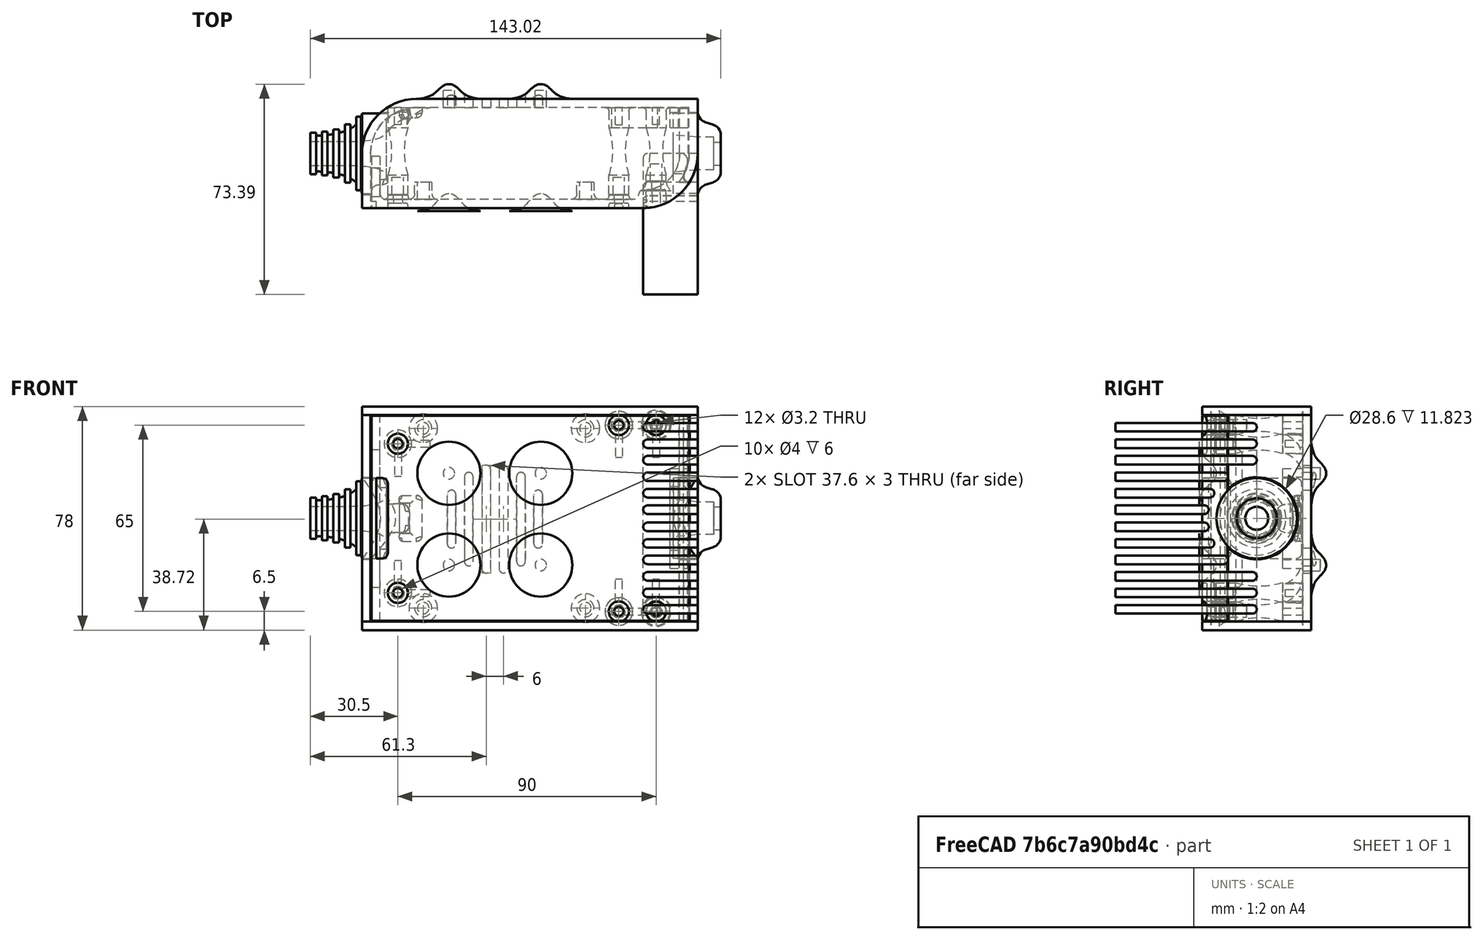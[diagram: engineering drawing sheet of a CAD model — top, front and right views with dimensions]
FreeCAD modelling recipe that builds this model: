
FCSTD DOCUMENT  (FreeCAD 0.19R0.19.2)
Label: enclosure_117
License: All rights reserved
LicenseURL: http://en.wikipedia.org/wiki/All_rights_reserved
objects: Part::Feature×72, Part::Revolution×72, Part::MultiFuse×53, Sketcher::SketchObject×32, Part::Fillet×24, Part::Cylinder×22, Part::Extrusion×21, Part::Cut×21, Part::Box×12, App::MeasureDistance×4
note: 329 computed .brp shape members not serialized (recipe doc carries the construction recipe); baked Part::Feature solids carry a one-line shape summary decoded from their .brp

FEATURE [Sketcher::SketchObject] Sketch  label="topSketch"
  FullyConstrained = true
  sketch-geometry (13):
    g0: LineSegment StartX=117 StartY=19 StartZ=0 EndX=117 EndY=38 EndZ=0
    g1: ArcOfCircle CenterX=98 CenterY=19 CenterZ=0 NormalX=0 NormalY=0 NormalZ=1 AngleXU=0 Radius=19 StartAngle=5.7297 EndAngle=6.28319
    g2: LineSegment StartX=0 StartY=3 StartZ=0 EndX=0 EndY=19 EndZ=0
    g3: LineSegment StartX=19 StartY=38 StartZ=0 EndX=117 EndY=38 EndZ=0
    g4: ArcOfCircle CenterX=19 CenterY=19 CenterZ=0 NormalX=0 NormalY=0 NormalZ=1 AngleXU=0 Radius=19 StartAngle=1.5708 EndAngle=3.14159
    g5: ArcOfCircle CenterX=19 CenterY=19 CenterZ=0 NormalX=0 NormalY=0 NormalZ=1 AngleXU=0 Radius=16 StartAngle=1.5708 EndAngle=3.14159
    g6: ArcOfCircle CenterX=98 CenterY=19 CenterZ=0 NormalX=0 NormalY=0 NormalZ=1 AngleXU=0 Radius=16 StartAngle=5.60905 EndAngle=6.28319
    g7: LineSegment StartX=114 StartY=19 StartZ=0 EndX=114 EndY=35 EndZ=0
    g8: LineSegment StartX=110.5 StartY=9.01251 StartZ=0 EndX=114.163 EndY=9.01251 EndZ=0
    g9: LineSegment StartX=114 StartY=35 StartZ=0 EndX=19 EndY=35 EndZ=0
    g10: LineSegment StartX=0 StartY=3 StartZ=0 EndX=0 EndY=0 EndZ=0
    g11: LineSegment StartX=3 StartY=0 StartZ=0 EndX=0 EndY=0 EndZ=0
    g12: LineSegment StartX=3 StartY=19 StartZ=0 EndX=3 EndY=0 EndZ=0
  constraints (33):
    c: Vertical(g0)
    c: Distance(g0) = 19
    c: Block(g0)
    c: Coincident(g1,g0)
    c: Block(g1)
    c: Vertical(g2)
    c: Block(g2)
    c: Coincident(g3,g0)
    c: Horizontal(g3)
    c: Distance(g3) = 98
    c: Coincident(g4,g3)
    c: Coincident(g4,g2)
    c: Block(g4)
    c: Coincident(g5,g4)
    c: Coincident(g6,g1)
    c: Block(g6)
    c: Block(g5)
    c: Coincident(g7,g6)
    c: Vertical(g7)
    c: Coincident(g8,g6)
    c: Coincident(g8,g1)
    c: Coincident(g9,g7)
    c: Coincident(g9,g5)
    c: Horizontal(g9)
    c: Tangent(g9,g5)
    c: Coincident(g10,g2)
    c: Distance(g10) = 3
    c: Vertical(g10)
    c: Coincident(g11,g10)
    c: Horizontal(g11)
    c: Coincident(g12,g5)
    c: Coincident(g12,g11)
    c: Vertical(g12)
FEATURE [Sketcher::SketchObject] Sketch001  label="bottomSketch"
  FullyConstrained = true
  sketch-geometry (32):
    g0: LineSegment StartX=3.3 StartY=-6.03275e-07 StartZ=0 EndX=98 EndY=-6.03275e-07 EndZ=0
    g1: ArcOfCircle CenterX=98 CenterY=19 CenterZ=0 NormalX=0 NormalY=0 NormalZ=1 AngleXU=0 Radius=19 StartAngle=4.71239 EndAngle=5.71103
    g2: LineSegment StartX=6.3 StartY=8 StartZ=0 EndX=3.3 EndY=8 EndZ=0
    g3: LineSegment StartX=3.3 StartY=8 StartZ=0 EndX=3.3 EndY=-6.03275e-07 EndZ=0
    g4: ArcOfCircle CenterX=8.3 CenterY=5 CenterZ=0 NormalX=0 NormalY=0 NormalZ=1 AngleXU=0 Radius=2 StartAngle=3.14159 EndAngle=4.71239
    g5: LineSegment StartX=6.3 StartY=8 StartZ=0 EndX=6.3 EndY=5 EndZ=0
    g6: ArcOfCircle CenterX=98 CenterY=19 CenterZ=0 NormalX=0 NormalY=0 NormalZ=1 AngleXU=0 Radius=12.7 StartAngle=4.71239 EndAngle=6.28319
    g7: LineSegment StartX=94.7 StartY=3 StartZ=0 EndX=8.3 EndY=3 EndZ=0
    g8-g12: Circle x5 (B-spline internal-alignment scaffolding for g13; pole/knot coordinates omitted)
    g13: BSplineCurve PolesCount=5 KnotsCount=3 Degree=3 IsPeriodic=0
    g14: GeomPoint X=98 Y=6.3 Z=0
    g15: GeomPoint X=96.3938 Y=4.71946 Z=0
    g16: GeomPoint X=94.7 Y=3 Z=0
    g17-g23: Circle x7 (B-spline internal-alignment scaffolding for g24; pole/knot coordinates omitted)
    g24: BSplineCurve PolesCount=7 KnotsCount=5 Degree=3 IsPeriodic=0
    g25-g29: GeomPoint x5 (B-spline internal-alignment scaffolding for g24; pole/knot coordinates omitted)
    g30: ArcOfCircle CenterX=98 CenterY=19 CenterZ=0 NormalX=0 NormalY=0 NormalZ=1 AngleXU=0 Radius=15.7 StartAngle=5.81226 EndAngle=6.28319
    g31: LineSegment StartX=110.7 StartY=19 StartZ=0 EndX=113.7 EndY=19 EndZ=0
  constraints (41):
    c: Horizontal(g0)
    c: Coincident(g1,g0)
    c: Block(g1)
    c: Horizontal(g2)
    c: Distance(g2) = 3
    c: Coincident(g3,g2)
    c: Vertical(g3)
    c: Coincident(g3,g0)
    c: Block(g4)
    c: Block(g2)
    c: Coincident(g5,g2)
    c: Coincident(g5,g4)
    c: Vertical(g5)
    c: Coincident(g6,g1)
    c: Block(g6)
    c: Coincident(g7,g4)
    c: Horizontal(g7)
    c: Block(g0)
    c: Block(g7)
    c: Block(g3)
    c: Coincident(g13,g6)
    c: Weight(g8) = 1
    c: Equal(g8, g9-g12) x4
    c: Coincident(g13,g7)
    c: InternalAlignment(g8-g12 -> g13) x5
    c: InternalAlignment(g14,g13)
    c: InternalAlignment(g15,g13)
    c: InternalAlignment(g16,g13)
    c: Block(g13)
    c: Weight(g17) = 1
    c: Equal(g17, g18-g23) x6
    c: Coincident(g24,g1)
    c: InternalAlignment(g17-g23 -> g24) x7
    c: InternalAlignment(g25-g29 -> g24) x5
    c: Block(g24)
    c: Coincident(g30,g24)
    c: Coincident(g31,g6)
    c: Coincident(g31,g30)
    c: Horizontal(g31)
    c: Block(g31)
    c: Block(g30)
FEATURE [Part::Extrusion] Extrude  label="top"
  Base = -> Sketch
  Dir = (0,0,1)
  DirMode = 2
  FaceMakerClass = Part::FaceMakerBullseye
  LengthFwd = 72
  LengthRev = 0
  Solid = true
  Symmetric = false
FEATURE [Part::Extrusion] Extrude001  label="bottom"
  Base = -> Sketch001
  Dir = (0,0,1)
  DirMode = 2
  FaceMakerClass = Part::FaceMakerBullseye
  LengthFwd = 71.4
  LengthRev = 0
  Placement = pos=(0,0,0.3) rot=(0,0,1;0rad)
  Solid = true
  Symmetric = false
FEATURE [Sketcher::SketchObject] Sketch002  label="topSketch001"
  FullyConstrained = true
  sketch-geometry (6):
    g0: LineSegment StartX=19 StartY=38 StartZ=0 EndX=117 EndY=38 EndZ=0
    g1: ArcOfCircle CenterX=19 CenterY=19 CenterZ=0 NormalX=0 NormalY=0 NormalZ=1 AngleXU=0 Radius=19 StartAngle=1.5708 EndAngle=3.14159
    g2: LineSegment StartX=117 StartY=38 StartZ=0 EndX=117 EndY=19 EndZ=0
    g3: LineSegment StartX=98 StartY=1.0161e-12 StartZ=0 EndX=5.22862e-06 EndY=1.0161e-12 EndZ=0
    g4: LineSegment StartX=5.22862e-06 StartY=19 StartZ=0 EndX=5.22862e-06 EndY=1.0161e-12 EndZ=0
    g5: ArcOfCircle CenterX=98 CenterY=19 CenterZ=0 NormalX=0 NormalY=0 NormalZ=1 AngleXU=0 Radius=19 StartAngle=4.71239 EndAngle=6.28319
  constraints (16):
    c: Horizontal(g0)
    c: Distance(g0) = 98
    c: Coincident(g1,g0)
    c: Block(g1)
    c: Coincident(g2,g0)
    c: Vertical(g2)
    c: Distance(g2) = 19
    c: Horizontal(g3)
    c: Coincident(g4,g1)
    c: Vertical(g4)
    c: Coincident(g3,g4)
    c: Block(g3)
    c: Coincident(g5,g2)
    c: Coincident(g5,g3)
    c: Block(g0)
    c: Block(g5)
FEATURE [Part::Extrusion] Extrude002  label="sideA"
  Base = -> Sketch002
  Dir = (0,0,1)
  DirMode = 2
  FaceMakerClass = Part::FaceMakerBullseye
  LengthFwd = 3
  LengthRev = 0
  Placement = pos=(0,0,-3) rot=(0,0,1;0rad)
  Solid = true
  Symmetric = false
FEATURE [Sketcher::SketchObject] Sketch003  label="topSketch002"
  FullyConstrained = true
  sketch-geometry (6):
    g0: LineSegment StartX=19 StartY=38 StartZ=0 EndX=117 EndY=38 EndZ=0
    g1: ArcOfCircle CenterX=19 CenterY=19 CenterZ=0 NormalX=0 NormalY=0 NormalZ=1 AngleXU=0 Radius=19 StartAngle=1.5708 EndAngle=3.14159
    g2: LineSegment StartX=117 StartY=38 StartZ=0 EndX=117 EndY=19 EndZ=0
    g3: LineSegment StartX=98 StartY=1.0161e-12 StartZ=0 EndX=5.22862e-06 EndY=1.0161e-12 EndZ=0
    g4: LineSegment StartX=5.22862e-06 StartY=19 StartZ=0 EndX=5.22862e-06 EndY=1.0161e-12 EndZ=0
    g5: ArcOfCircle CenterX=98 CenterY=19 CenterZ=0 NormalX=0 NormalY=0 NormalZ=1 AngleXU=0 Radius=19 StartAngle=4.71239 EndAngle=6.28319
  constraints (16):
    c: Horizontal(g0)
    c: Distance(g0) = 98
    c: Coincident(g1,g0)
    c: Block(g1)
    c: Coincident(g2,g0)
    c: Vertical(g2)
    c: Distance(g2) = 19
    c: Horizontal(g3)
    c: Coincident(g4,g1)
    c: Vertical(g4)
    c: Coincident(g3,g4)
    c: Block(g3)
    c: Coincident(g5,g2)
    c: Coincident(g5,g3)
    c: Block(g0)
    c: Block(g5)
FEATURE [Part::Extrusion] Extrude003  label="sideB"
  Base = -> Sketch003
  Dir = (0,0,1)
  DirMode = 2
  FaceMakerClass = Part::FaceMakerBullseye
  LengthFwd = 3
  LengthRev = 0
  Placement = pos=(0,0,72) rot=(0,0,1;0rad)
  Solid = true
  Symmetric = false
FEATURE [Sketcher::SketchObject] Sketch004
  FullyConstrained = true
  MapMode = 3
  Placement = pos=(0,0,0) rot=(1,0,0;1.5708rad)
  Support = -> [Extrude]
  sketch-geometry (8):
    g0: Circle CenterX=80.351 CenterY=-67.6202 CenterZ=0 NormalX=0 NormalY=0 NormalZ=1 AngleXU=0 Radius=2
    g1: Circle CenterX=80.351 CenterY=-67.6202 CenterZ=0 NormalX=0 NormalY=0 NormalZ=1 AngleXU=0 Radius=3
    g2: Circle CenterX=80.351 CenterY=-4.92017 CenterZ=0 NormalX=0 NormalY=0 NormalZ=1 AngleXU=0 Radius=2
    g3: Circle CenterX=80.351 CenterY=-4.92017 CenterZ=0 NormalX=0 NormalY=0 NormalZ=1 AngleXU=0 Radius=3
    g4: Circle CenterX=23.851 CenterY=-4.92017 CenterZ=0 NormalX=0 NormalY=0 NormalZ=1 AngleXU=0 Radius=2
    g5: Circle CenterX=23.851 CenterY=-4.92017 CenterZ=0 NormalX=0 NormalY=0 NormalZ=1 AngleXU=0 Radius=3
    g6: Circle CenterX=23.851 CenterY=-67.6202 CenterZ=0 NormalX=0 NormalY=0 NormalZ=1 AngleXU=0 Radius=2
    g7: Circle CenterX=23.851 CenterY=-67.6202 CenterZ=0 NormalX=0 NormalY=0 NormalZ=1 AngleXU=0 Radius=3
  constraints (8):
    c: Block(g3)
    c: Block(g2)
    c: Block(g1)
    c: Block(g0)
    c: Block(g6)
    c: Block(g7)
    c: Block(g4)
    c: Block(g5)
FEATURE [Part::Extrusion] Extrude004
  Base = -> Sketch004
  Dir = (0,-1,2e-16)
  DirMode = 2
  FaceMakerClass = Part::FaceMakerBullseye
  LengthFwd = 6
  LengthRev = 0
  Placement = pos=(0,9,0) rot=(0,0,1;0rad)
  Solid = true
  Symmetric = false
FEATURE [Sketcher::SketchObject] Sketch005
  FullyConstrained = true
  MapMode = 3
  Placement = pos=(0,0,0) rot=(1,0,0;1.5708rad)
  Support = -> [Extrude]
  sketch-geometry (8):
    g0: Circle CenterX=80.351 CenterY=-67.6202 CenterZ=0 NormalX=0 NormalY=0 NormalZ=1 AngleXU=0 Radius=3
    g1: Circle CenterX=80.351 CenterY=-4.92017 CenterZ=0 NormalX=0 NormalY=0 NormalZ=1 AngleXU=0 Radius=3
    g2: Circle CenterX=23.851 CenterY=-4.92017 CenterZ=0 NormalX=0 NormalY=0 NormalZ=1 AngleXU=0 Radius=3
    g3: Circle CenterX=23.851 CenterY=-67.6202 CenterZ=0 NormalX=0 NormalY=0 NormalZ=1 AngleXU=0 Radius=3
    g4: Circle CenterX=23.851 CenterY=-67.6202 CenterZ=0 NormalX=0 NormalY=0 NormalZ=1 AngleXU=0 Radius=5
    g5: Circle CenterX=80.351 CenterY=-67.6202 CenterZ=0 NormalX=0 NormalY=0 NormalZ=1 AngleXU=0 Radius=5
    g6: Circle CenterX=23.851 CenterY=-4.92017 CenterZ=0 NormalX=0 NormalY=0 NormalZ=1 AngleXU=0 Radius=5
    g7: Circle CenterX=80.351 CenterY=-4.92017 CenterZ=0 NormalX=0 NormalY=0 NormalZ=1 AngleXU=0 Radius=5
  constraints (8):
    c: Block(g1)
    c: Block(g0)
    c: Block(g3)
    c: Block(g2)
    c: Block(g5)
    c: Block(g4)
    c: Block(g6)
    c: Block(g7)
FEATURE [Part::Extrusion] Extrude005
  Base = -> Sketch005
  Dir = (0,-1,2e-16)
  DirMode = 2
  FaceMakerClass = Part::FaceMakerBullseye
  LengthFwd = 2
  LengthRev = 0
  Solid = true
  Symmetric = false
FEATURE [Sketcher::SketchObject] Sketch006
  FullyConstrained = true
  MapMode = 3
  Placement = pos=(0,0,0) rot=(1,0,0;1.5708rad)
  sketch-geometry (8):
    g0: Circle CenterX=80.351 CenterY=-67.6202 CenterZ=0 NormalX=0 NormalY=0 NormalZ=1 AngleXU=0 Radius=3
    g1: Circle CenterX=80.351 CenterY=-4.92017 CenterZ=0 NormalX=0 NormalY=0 NormalZ=1 AngleXU=0 Radius=3
    g2: Circle CenterX=23.851 CenterY=-4.92017 CenterZ=0 NormalX=0 NormalY=0 NormalZ=1 AngleXU=0 Radius=3
    g3: Circle CenterX=23.851 CenterY=-67.6202 CenterZ=0 NormalX=0 NormalY=0 NormalZ=1 AngleXU=0 Radius=3
    g4: Circle CenterX=23.851 CenterY=-67.6202 CenterZ=0 NormalX=0 NormalY=0 NormalZ=1 AngleXU=0 Radius=5
    g5: Circle CenterX=80.351 CenterY=-67.6202 CenterZ=0 NormalX=0 NormalY=0 NormalZ=1 AngleXU=0 Radius=5
    g6: Circle CenterX=23.851 CenterY=-4.92017 CenterZ=0 NormalX=0 NormalY=0 NormalZ=1 AngleXU=0 Radius=5
    g7: Circle CenterX=80.351 CenterY=-4.92017 CenterZ=0 NormalX=0 NormalY=0 NormalZ=1 AngleXU=0 Radius=5
  constraints (8):
    c: Block(g1)
    c: Block(g0)
    c: Block(g3)
    c: Block(g2)
    c: Block(g5)
    c: Block(g4)
    c: Block(g6)
    c: Block(g7)
FEATURE [Part::Extrusion] Extrude007
  Base = -> Sketch006
  Dir = (0,-1,2e-16)
  DirMode = 2
  FaceMakerClass = Part::FaceMakerBullseye
  LengthFwd = 2
  LengthRev = 0
  Solid = true
  Symmetric = false
FEATURE [Part::Fillet] Fillet
  Base = -> Extrude007
  Edges = 4 edges r=1.99: [Edge6,Edge12,Edge18,Edge24]
FEATURE [Part::Cut] Cut
  Base = -> Extrude005
  Placement = pos=(0,5,0) rot=(0,0,1;0rad)
  Tool = -> Fillet
FEATURE [Part::MultiFuse] Fusion  label="pCBScrews"
  Placement = pos=(-2.5,0,72.3) rot=(0,0,1;0rad)
  Shapes = -> [Extrude004,Cut]
FEATURE [App::MeasureDistance] Distance  label="Distance: 0.69 mm"
  Distance = 0.685967
  P1 = (24.0138,2.9647,0.3)
  P2 = (23.8901,3,-0.373787)
FEATURE [App::MeasureDistance] Distance001  label="Distance: 0.53 mm"
  Distance = 0.533607
  P1 = (80.2939,3,72.2334)
  P2 = (80.281,2.99661,71.7)
FEATURE [Part::Fillet] Fillet001
  Base = -> Extrude001
  Edges = 1 edges r=2.4: [Edge17]
FEATURE [Part::Fillet] Fillet002  label="bottom001"
  Base = -> Fillet001
  Edges = 1 edges r=2.4: [Edge36]
FEATURE [Part::Fillet] Fillet003  label="top001"
  Base = -> Extrude
  Edges = 1 edges r=2: [Edge1]
FEATURE [Sketcher::SketchObject] Sketch007
  FullyConstrained = true
  sketch-geometry (16):
    g0: LineSegment StartX=4 StartY=0 StartZ=0 EndX=4 EndY=2.4 EndZ=0
    g1: LineSegment StartX=4 StartY=2.4 StartZ=0 EndX=7 EndY=2.4 EndZ=0
    g2: LineSegment StartX=4 StartY=0 StartZ=0 EndX=5.7 EndY=0 EndZ=0
    g3: LineSegment StartX=5.7 StartY=0 StartZ=0 EndX=5.7 EndY=-5.6 EndZ=0
    g4-g8: Circle x5 (B-spline internal-alignment scaffolding for g9; pole/knot coordinates omitted)
    g9: BSplineCurve PolesCount=5 KnotsCount=3 Degree=3 IsPeriodic=0
    g10: GeomPoint X=7 Y=2.4 Z=0
    g11: GeomPoint X=10.4582 Y=-1.55472 Z=0
    g12: GeomPoint X=14 Y=-5.6 Z=0
    g13: LineSegment StartX=14 StartY=-5.6 StartZ=0 EndX=14 EndY=-14.1 EndZ=0
    g14: LineSegment StartX=14 StartY=-14.1 StartZ=0 EndX=6.5 EndY=-14.1 EndZ=0
    g15: LineSegment StartX=5.7 StartY=-5.6 StartZ=0 EndX=6.5 EndY=-14.1 EndZ=0
  constraints (28):
    c: Distance(g0) = 2.4
    c: Vertical(g0)
    c: Block(g0)
    c: Coincident(g1,g0)
    c: Horizontal(g1)
    c: Distance(g1) = 3
    c: Coincident(g2,g0)
    c: Horizontal(g2)
    c: Distance(g2) = 1.7
    c: Coincident(g3,g2)
    c: Vertical(g3)
    c: Distance(g3) = 5.6
    c: Coincident(g9,g1)
    c: Weight(g4) = 1
    c: Equal(g4, g5-g8) x4
    c: InternalAlignment(g4-g8 -> g9) x5
    c: InternalAlignment(g10,g9)
    c: InternalAlignment(g11,g9)
    c: InternalAlignment(g12,g9)
    c: Block(g9)
    c: Coincident(g13,g9)
    c: Vertical(g13)
    c: Distance(g13) = 8.5
    c: Coincident(g14,g13)
    c: Horizontal(g14)
    c: Distance(g14) = 7.5
    c: Coincident(g15,g3)
    c: Coincident(g15,g14)
FEATURE [Part::Feature] Face
  shape: bbox 10 x 16.5 x 2e-07 mm, 1 faces, 0 solids (baked)
FEATURE [Part::Revolution] Revolve  label="plugHousing"
  Angle = 360
  Axis = (0,1,0)
  Base = (0,0,0)
  FaceMakerClass = Part::FaceMakerBullseye
  Placement = pos=(0,0,36.15) rot=(0,0,1;0rad)
  Solid = false
  Source = -> Face
  Symmetric = false
FEATURE [Part::Feature] Face001
  shape: bbox 10 x 16.5 x 2e-07 mm, 1 faces, 0 solids (baked)
FEATURE [Part::Revolution] Revolve001  label="plugHousing001"
  Angle = 360
  Axis = (0,1,0)
  Base = (0,0,0)
  FaceMakerClass = Part::FaceMakerBullseye
  Placement = pos=(0,0,36.15) rot=(0,0,1;0rad)
  Solid = false
  Source = -> Face001
  Symmetric = false
FEATURE [Part::MultiFuse] Fusion001  label="plugHousing002"
  Placement = pos=(0,0,0) rot=(0,0,1;1.5708rad)
  Shapes = -> [Revolve001,Revolve]
FEATURE [Part::Feature] Face002
  shape: bbox 10 x 16.5 x 2e-07 mm, 1 faces, 0 solids (baked)
FEATURE [Part::Revolution] Revolve003  label="plugHousing005"
  Angle = 360
  Axis = (0,1,0)
  Base = (0,0,0)
  FaceMakerClass = Part::FaceMakerBullseye
  Placement = pos=(0,0,36.15) rot=(0,0,1;0rad)
  Solid = false
  Source = -> Face002
  Symmetric = false
FEATURE [Part::Feature] Face003
  shape: bbox 10 x 16.5 x 2e-07 mm, 1 faces, 0 solids (baked)
FEATURE [Part::Revolution] Revolve002  label="plugHousing003"
  Angle = 360
  Axis = (0,1,0)
  Base = (0,0,0)
  FaceMakerClass = Part::FaceMakerBullseye
  Placement = pos=(0,0,36.15) rot=(0,0,1;0rad)
  Solid = false
  Source = -> Face003
  Symmetric = false
FEATURE [Part::MultiFuse] Fusion002  label="plugHousing004"
  Placement = pos=(0,0,0) rot=(0,0,1;1.5708rad)
  Shapes = -> [Revolve002,Revolve003]
FEATURE [Part::MultiFuse] Fusion003  label="plugHousing006"
  Placement = pos=(0,19,0) rot=(0,0,1;3.14159rad)
  Shapes = -> [Fusion002,Fusion001]
FEATURE [Part::Feature] Face004
  shape: bbox 10 x 16.5 x 2e-07 mm, 1 faces, 0 solids (baked)
FEATURE [Part::Revolution] Revolve006  label="plugHousing010"
  Angle = 360
  Axis = (0,1,0)
  Base = (0,0,0)
  FaceMakerClass = Part::FaceMakerBullseye
  Placement = pos=(0,0,36.15) rot=(0,0,1;0rad)
  Solid = false
  Source = -> Face004
  Symmetric = false
FEATURE [Part::Feature] Face005
  shape: bbox 10 x 16.5 x 2e-07 mm, 1 faces, 0 solids (baked)
FEATURE [Part::Revolution] Revolve007  label="plugHousing011"
  Angle = 360
  Axis = (0,1,0)
  Base = (0,0,0)
  FaceMakerClass = Part::FaceMakerBullseye
  Placement = pos=(0,0,36.15) rot=(0,0,1;0rad)
  Solid = false
  Source = -> Face005
  Symmetric = false
FEATURE [Part::Feature] Face006
  shape: bbox 10 x 16.5 x 2e-07 mm, 1 faces, 0 solids (baked)
FEATURE [Part::Revolution] Revolve004  label="plugHousing007"
  Angle = 360
  Axis = (0,1,0)
  Base = (0,0,0)
  FaceMakerClass = Part::FaceMakerBullseye
  Placement = pos=(0,0,36.15) rot=(0,0,1;0rad)
  Solid = false
  Source = -> Face006
  Symmetric = false
FEATURE [Part::MultiFuse] Fusion004  label="plugHousing009"
  Placement = pos=(0,0,0) rot=(0,0,1;1.5708rad)
  Shapes = -> [Revolve004,Revolve007]
FEATURE [Part::Feature] Face007
  shape: bbox 10 x 16.5 x 2e-07 mm, 1 faces, 0 solids (baked)
FEATURE [Part::Revolution] Revolve005  label="plugHousing008"
  Angle = 360
  Axis = (0,1,0)
  Base = (0,0,0)
  FaceMakerClass = Part::FaceMakerBullseye
  Placement = pos=(0,0,36.15) rot=(0,0,1;0rad)
  Solid = false
  Source = -> Face007
  Symmetric = false
FEATURE [Part::MultiFuse] Fusion005  label="plugHousing012"
  Placement = pos=(0,0,0) rot=(0,0,1;1.5708rad)
  Shapes = -> [Revolve006,Revolve005]
FEATURE [Part::MultiFuse] Fusion006  label="plugHousing013"
  Placement = pos=(0,19,0) rot=(0,0,1;3.14159rad)
  Shapes = -> [Fusion005,Fusion004]
FEATURE [Part::MultiFuse] Fusion007  label="plugHousing014"
  Placement = pos=(122.621,0,-0.15) rot=(0,0,1;0rad)
  Shapes = -> [Fusion003,Fusion006]
FEATURE [Part::Cylinder] Cylinder002
  Angle = 360
  AttacherType = Attacher::AttachEngine3D
  Height = 20
  Placement = pos=(0,0,36.15) rot=(0,0,1;0rad)
  Radius = 4
FEATURE [Part::Cylinder] Cylinder003
  Angle = 360
  AttacherType = Attacher::AttachEngine3D
  Height = 10
  Placement = pos=(0,0,36.15) rot=(0,0,1;0rad)
  Radius = 4
FEATURE [Part::MultiFuse] Fusion009  label="removeToCreateHoleForPlugHousing"
  Placement = pos=(70,19,36.15) rot=(0,1,0;1.5708rad)
  Shapes = -> [Cylinder002,Cylinder003]
FEATURE [Part::Cylinder] Cylinder004
  Angle = 360
  AttacherType = Attacher::AttachEngine3D
  Height = 20
  Placement = pos=(0,0,36.15) rot=(0,0,1;0rad)
  Radius = 4
FEATURE [Part::Cylinder] Cylinder005
  Angle = 360
  AttacherType = Attacher::AttachEngine3D
  Height = 10
  Placement = pos=(0,0,36.15) rot=(0,0,1;0rad)
  Radius = 4
FEATURE [Part::MultiFuse] Fusion010  label="removeToCreateHoleForPlugHousing001"
  Placement = pos=(70,19,36.15) rot=(0,1,0;1.5708rad)
  Shapes = -> [Cylinder004,Cylinder005]
FEATURE [Part::Cut] Cut001
  Base = -> Fillet003
  Tool = -> Fusion010
FEATURE [Part::Cut] Cut002  label="Bottom"
  Base = -> Fillet002
  Tool = -> Fusion009
FEATURE [Part::Feature] Face008
  shape: bbox 10 x 16.5 x 2e-07 mm, 1 faces, 0 solids (baked)
FEATURE [Part::Revolution] Revolve011  label="plugHousing021"
  Angle = 360
  Axis = (0,1,0)
  Base = (0,0,0)
  FaceMakerClass = Part::FaceMakerBullseye
  Placement = pos=(0,0,36.15) rot=(0,0,1;0rad)
  Solid = false
  Source = -> Face008
  Symmetric = false
FEATURE [Part::Feature] Face009
  shape: bbox 10 x 16.5 x 2e-07 mm, 1 faces, 0 solids (baked)
FEATURE [Part::Revolution] Revolve012  label="plugHousing022"
  Angle = 360
  Axis = (0,1,0)
  Base = (0,0,0)
  FaceMakerClass = Part::FaceMakerBullseye
  Placement = pos=(0,0,36.15) rot=(0,0,1;0rad)
  Solid = false
  Source = -> Face009
  Symmetric = false
FEATURE [Part::Feature] Face010 .. Face013  x4 (patterned run collapsed; names and placements below)
  shape: bbox 10 x 16.5 x 2e-07 mm, 1 faces, 0 solids (baked)
FEATURE [Part::Revolution] Revolve015  label="plugHousing027"
  Angle = 360
  Axis = (0,1,0)
  Base = (0,0,0)
  FaceMakerClass = Part::FaceMakerBullseye
  Placement = pos=(0,0,36.15) rot=(0,0,1;0rad)
  Solid = false
  Source = -> Face013
  Symmetric = false
FEATURE [Part::Feature] Face014
  shape: bbox 10 x 16.5 x 2e-07 mm, 1 faces, 0 solids (baked)
FEATURE [Part::Feature] Face015
  shape: bbox 10 x 16.5 x 2e-07 mm, 1 faces, 0 solids (baked)
FEATURE [Part::Feature] Face016
  shape: bbox 10 x 16.5 x 2e-07 mm, 1 faces, 0 solids (baked)
FEATURE [Part::Revolution] Revolve019  label="plugHousing033"
  Angle = 360
  Axis = (0,1,0)
  Base = (0,0,0)
  FaceMakerClass = Part::FaceMakerBullseye
  Placement = pos=(0,0,36.15) rot=(0,0,1;0rad)
  Solid = false
  Source = -> Face016
  Symmetric = false
FEATURE [Part::Feature] Face017
  shape: bbox 10 x 16.5 x 2e-07 mm, 1 faces, 0 solids (baked)
FEATURE [Part::Revolution] Revolve020  label="plugHousing034"
  Angle = 360
  Axis = (0,1,0)
  Base = (0,0,0)
  FaceMakerClass = Part::FaceMakerBullseye
  Placement = pos=(0,0,36.15) rot=(0,0,1;0rad)
  Solid = false
  Source = -> Face017
  Symmetric = false
FEATURE [Part::Feature] Face018
  shape: bbox 10 x 16.5 x 2e-07 mm, 1 faces, 0 solids (baked)
FEATURE [Part::Revolution] Revolve016  label="plugHousing030"
  Angle = 360
  Axis = (0,1,0)
  Base = (0,0,0)
  FaceMakerClass = Part::FaceMakerBullseye
  Placement = pos=(0,0,36.15) rot=(0,0,1;0rad)
  Solid = false
  Source = -> Face018
  Symmetric = false
FEATURE [Part::MultiFuse] Fusion020  label="plugHousing038"
  Placement = pos=(0,0,0) rot=(0,0,1;1.5708rad)
  Shapes = -> [Revolve016,Revolve020]
FEATURE [Part::Feature] Face019
  shape: bbox 10 x 16.5 x 2e-07 mm, 1 faces, 0 solids (baked)
FEATURE [Part::Feature] Face020
  shape: bbox 10 x 16.5 x 2e-07 mm, 1 faces, 0 solids (baked)
FEATURE [Part::Revolution] Revolve017  label="plugHousing031"
  Angle = 360
  Axis = (0,1,0)
  Base = (0,0,0)
  FaceMakerClass = Part::FaceMakerBullseye
  Placement = pos=(0,0,36.15) rot=(0,0,1;0rad)
  Solid = false
  Source = -> Face020
  Symmetric = false
FEATURE [Part::MultiFuse] Fusion021  label="plugHousing039"
  Placement = pos=(0,0,0) rot=(0,0,1;1.5708rad)
  Shapes = -> [Revolve019,Revolve017]
FEATURE [Part::MultiFuse] Fusion023  label="plugHousing041"
  Placement = pos=(0,19,0) rot=(0,0,1;3.14159rad)
  Shapes = -> [Fusion021,Fusion020]
FEATURE [Part::Revolution] Revolve022  label="plugHousing043"
  Angle = 360
  Axis = (0,1,0)
  Base = (0,0,0)
  FaceMakerClass = Part::FaceMakerBullseye
  Placement = pos=(0,0,36.15) rot=(0,0,1;0rad)
  Solid = false
  Source = -> Face019
  Symmetric = false
FEATURE [Part::Feature] Face021
  shape: bbox 10 x 16.5 x 2e-07 mm, 1 faces, 0 solids (baked)
FEATURE [Part::Revolution] Revolve023  label="plugHousing044"
  Angle = 360
  Axis = (0,1,0)
  Base = (0,0,0)
  FaceMakerClass = Part::FaceMakerBullseye
  Placement = pos=(0,0,36.15) rot=(0,0,1;0rad)
  Solid = false
  Source = -> Face021
  Symmetric = false
FEATURE [Part::Feature] Face022
  shape: bbox 10 x 16.5 x 2e-07 mm, 1 faces, 0 solids (baked)
FEATURE [Part::Revolution] Revolve018  label="plugHousing032"
  Angle = 360
  Axis = (0,1,0)
  Base = (0,0,0)
  FaceMakerClass = Part::FaceMakerBullseye
  Placement = pos=(0,0,36.15) rot=(0,0,1;0rad)
  Solid = false
  Source = -> Face022
  Symmetric = false
FEATURE [Part::MultiFuse] Fusion022  label="plugHousing040"
  Placement = pos=(0,0,0) rot=(0,0,1;1.5708rad)
  Shapes = -> [Revolve018,Revolve023]
FEATURE [Part::Feature] Face023
  shape: bbox 10 x 16.5 x 2e-07 mm, 1 faces, 0 solids (baked)
FEATURE [Part::Revolution] Revolve021  label="plugHousing035"
  Angle = 360
  Axis = (0,1,0)
  Base = (0,0,0)
  FaceMakerClass = Part::FaceMakerBullseye
  Placement = pos=(0,0,36.15) rot=(0,0,1;0rad)
  Solid = false
  Source = -> Face023
  Symmetric = false
FEATURE [Part::MultiFuse] Fusion018  label="plugHousing036"
  Placement = pos=(0,0,0) rot=(0,0,1;1.5708rad)
  Shapes = -> [Revolve022,Revolve021]
FEATURE [Part::MultiFuse] Fusion019  label="plugHousing037"
  Placement = pos=(0,19,0) rot=(0,0,1;3.14159rad)
  Shapes = -> [Fusion018,Fusion022]
FEATURE [Part::MultiFuse] Fusion024  label="plugHousing042"
  Placement = pos=(122.621,0,-0.15) rot=(0,0,1;0rad)
  Shapes = -> [Fusion023,Fusion019]
FEATURE [Part::Cylinder] Cylinder006
  Angle = 360
  AttacherType = Attacher::AttachEngine3D
  Height = 20
  Placement = pos=(0,0,36.15) rot=(0,0,1;0rad)
  Radius = 14.3
FEATURE [Part::Cylinder] Cylinder007
  Angle = 360
  AttacherType = Attacher::AttachEngine3D
  Height = 10
  Placement = pos=(0,0,36.15) rot=(0,0,1;0rad)
  Radius = 4
FEATURE [Part::MultiFuse] Fusion026  label="removeToCreteHoleForPlugHousing"
  Placement = pos=(70,19,36) rot=(0,1,0;1.5708rad)
  Shapes = -> [Cylinder006,Cylinder007]
FEATURE [Part::Box] Box001  label="Cube001"
  AttacherType = Attacher::AttachEngine3D
  Height = 28
  Length = 3
  Placement = pos=(110.7,19,22) rot=(0,0,1;0rad)
  Width = 15.7
FEATURE [Part::Cut] Cut003  label="top002"
  Base = -> Cut001
  Tool = -> Fusion007
FEATURE [Part::Revolution] Revolve008  label="plugHousing015"
  Angle = 360
  Axis = (0,1,0)
  Base = (0,0,0)
  FaceMakerClass = Part::FaceMakerBullseye
  Placement = pos=(0,0,36.15) rot=(0,0,1;0rad)
  Solid = false
  Source = -> Face010
  Symmetric = false
FEATURE [Part::MultiFuse] Fusion013  label="plugHousing020"
  Placement = pos=(0,0,0) rot=(0,0,1;1.5708rad)
  Shapes = -> [Revolve008,Revolve012]
FEATURE [Part::Cut] Cut004  label="top003"
  Base = -> Cut003
  Placement = pos=(1,0,0) rot=(0,0,1;0rad)
  Tool = -> Fusion026
FEATURE [Part::Cylinder] Cylinder008
  Angle = 360
  AttacherType = Attacher::AttachEngine3D
  Height = 20
  Placement = pos=(0,0,36.15) rot=(0,0,1;0rad)
  Radius = 10.3
FEATURE [Part::Cylinder] Cylinder009
  Angle = 360
  AttacherType = Attacher::AttachEngine3D
  Height = 10
  Placement = pos=(0,0,36.15) rot=(0,0,1;0rad)
  Radius = 4
FEATURE [Part::MultiFuse] Fusion027  label="removeToCreteHoleForPlugHousing001"
  Placement = pos=(70,19,36) rot=(0,1,0;1.5708rad)
  Shapes = -> [Cylinder008,Cylinder009]
FEATURE [Part::Cut] Cut005  label="plugHousingTab"
  Base = -> Box001
  Tool = -> Fusion027
FEATURE [Part::MultiFuse] Fusion028  label="plugHousing045"
  Shapes = -> [Fusion024,Cut005]
FEATURE [Part::Box] Box002  label="Cube002"
  AttacherType = Attacher::AttachEngine3D
  Height = 28.8
  Length = 3
  Placement = pos=(107.3,28,21.6) rot=(0,0,1;0rad)
  Width = 7
FEATURE [Part::Box] Box003  label="Cube003"
  AttacherType = Attacher::AttachEngine3D
  Height = 3
  Length = 6.4
  Placement = pos=(107.3,28,18.6) rot=(0,0,1;0rad)
  Width = 7
FEATURE [Part::Box] Box004  label="Cube004"
  AttacherType = Attacher::AttachEngine3D
  Height = 3
  Length = 6.4
  Placement = pos=(107.3,28,50.4) rot=(0,0,1;0rad)
  Width = 7
FEATURE [Part::MultiFuse] Fusion029  label="plugHousingBracketHolder"
  Shapes = -> [Box004,Box002,Box003]
FEATURE [Part::Cylinder] Cylinder010
  Angle = 360
  AttacherType = Attacher::AttachEngine3D
  Height = 20
  Placement = pos=(0,0,36.15) rot=(0,0,1;0rad)
  Radius = 14.3
FEATURE [Part::Cylinder] Cylinder011
  Angle = 360
  AttacherType = Attacher::AttachEngine3D
  Height = 10
  Placement = pos=(0,0,36.15) rot=(0,0,1;0rad)
  Radius = 4
FEATURE [Part::MultiFuse] Fusion030  label="removeToCreteHoleForPlugHousing002"
  Placement = pos=(70,19,36) rot=(0,1,0;1.5708rad)
  Shapes = -> [Cylinder010,Cylinder011]
FEATURE [Part::Cut] Cut006  label="plugHousingBracketHolder001"
  Base = -> Fusion029
  Tool = -> Fusion030
FEATURE [Part::Cylinder] Cylinder012
  Angle = 360
  AttacherType = Attacher::AttachEngine3D
  Height = 20
  Placement = pos=(0,0,36.15) rot=(0,0,1;0rad)
  Radius = 7
FEATURE [Part::Cylinder] Cylinder013
  Angle = 360
  AttacherType = Attacher::AttachEngine3D
  Height = 10
  Placement = pos=(0,0,36.15) rot=(0,0,1;0rad)
  Radius = 4
FEATURE [Part::MultiFuse] Fusion032  label="removeToCreteHoleForPlugHousing003"
  Placement = pos=(70,19,36) rot=(0,1,0;1.5708rad)
  Shapes = -> [Cylinder012,Cylinder013]
FEATURE [Part::Cut] Cut007  label="bottom002"
  Base = -> Cut002
  Tool = -> Fusion032
FEATURE [Sketcher::SketchObject] Sketch008
  FullyConstrained = true
  sketch-geometry (54):
    g0: LineSegment StartX=-4.2 StartY=0 StartZ=0 EndX=-6.2 EndY=0 EndZ=0
    g1: LineSegment StartX=-14 StartY=-18 StartZ=0 EndX=-14 EndY=-26.5 EndZ=0
    g2: LineSegment StartX=-4.2 StartY=0 StartZ=0 EndX=-4.2 EndY=-13.4877 EndZ=0
    g3: Circle CenterX=-4.2 CenterY=-13.4877 CenterZ=0 NormalX=0 NormalY=0 NormalZ=1 AngleXU=0 Radius=1
    g4: Circle CenterX=-4.2 CenterY=-26.5 CenterZ=0 NormalX=0 NormalY=0 NormalZ=1 AngleXU=0 Radius=1
    g5: Circle CenterX=-8.2 CenterY=-26.5 CenterZ=0 NormalX=0 NormalY=0 NormalZ=1 AngleXU=0 Radius=1
    g6: BSplineCurve PolesCount=3 KnotsCount=2 Degree=2 IsPeriodic=0
    g7: GeomPoint X=-4.2 Y=-13.4877 Z=0
    g8: GeomPoint X=-8.2 Y=-26.5 Z=0
    g9: LineSegment StartX=-14 StartY=-26.5 StartZ=0 EndX=-8.2 EndY=-26.5 EndZ=0
    g10: LineSegment StartX=-10.15 StartY=-12 StartZ=0 EndX=-10.15 EndY=-14 EndZ=0
    g11: LineSegment StartX=-12.8401 StartY=-16 StartZ=0 EndX=-10.1571 EndY=-16 EndZ=0
    g12: LineSegment StartX=-10.15 StartY=-14 StartZ=0 EndX=-8.70761 EndY=-14 EndZ=0
    g13: LineSegment StartX=-12.8401 StartY=-16 StartZ=0 EndX=-12.8401 EndY=-17.6958 EndZ=0
    g14: LineSegment StartX=-10.15 StartY=-12 StartZ=0 EndX=-7.79258 EndY=-12 EndZ=0
    g15: Circle CenterX=-6.2215 CenterY=-2 CenterZ=0 NormalX=0 NormalY=0 NormalZ=1 AngleXU=0 Radius=1
    g16: Circle CenterX=-6.22762 CenterY=-2.58724 CenterZ=0 NormalX=0 NormalY=0 NormalZ=1 AngleXU=0 Radius=1
    g17: Circle CenterX=-6.32538 CenterY=-4 CenterZ=0 NormalX=0 NormalY=0 NormalZ=1 AngleXU=0 Radius=1
    g18: BSplineCurve PolesCount=3 KnotsCount=2 Degree=2 IsPeriodic=0
    g19: GeomPoint X=-6.2215 Y=-2 Z=0
    g20: GeomPoint X=-6.32538 Y=-4 Z=0
    g21: Circle CenterX=-6.48644 CenterY=-5.99526 CenterZ=0 NormalX=0 NormalY=0 NormalZ=1 AngleXU=0 Radius=1
    g22: Circle CenterX=-6.58486 CenterY=-6.99526 CenterZ=0 NormalX=0 NormalY=0 NormalZ=1 AngleXU=0 Radius=1
    g23: Circle CenterX=-6.77343 CenterY=-8 CenterZ=0 NormalX=0 NormalY=0 NormalZ=1 AngleXU=0 Radius=1
    g24: BSplineCurve PolesCount=3 KnotsCount=2 Degree=2 IsPeriodic=0
    g25: GeomPoint X=-6.48644 Y=-5.99526 Z=0
    g26: GeomPoint X=-6.77343 Y=-8 Z=0
    g27: Circle CenterX=-7.19003 CenterY=-10 CenterZ=0 NormalX=0 NormalY=0 NormalZ=1 AngleXU=0 Radius=1
    g28: Circle CenterX=-7.44407 CenterY=-11.0915 CenterZ=0 NormalX=0 NormalY=0 NormalZ=1 AngleXU=0 Radius=1
    g29: Circle CenterX=-7.79258 CenterY=-12 CenterZ=0 NormalX=0 NormalY=0 NormalZ=1 AngleXU=0 Radius=1
    g30: BSplineCurve PolesCount=3 KnotsCount=2 Degree=2 IsPeriodic=0
    g31: GeomPoint X=-7.19003 Y=-10 Z=0
    g32: GeomPoint X=-7.79258 Y=-12 Z=0
    g33: Circle CenterX=-8.70761 CenterY=-14 CenterZ=0 NormalX=0 NormalY=0 NormalZ=1 AngleXU=0 Radius=1
    g34: Circle CenterX=-9.33087 CenterY=-15.1837 CenterZ=0 NormalX=0 NormalY=0 NormalZ=1 AngleXU=0 Radius=1
    g35: Circle CenterX=-10.1571 CenterY=-16 CenterZ=0 NormalX=0 NormalY=0 NormalZ=1 AngleXU=0 Radius=1
    g36: BSplineCurve PolesCount=3 KnotsCount=2 Degree=2 IsPeriodic=0
    g37: GeomPoint X=-8.70761 Y=-14 Z=0
    g38: GeomPoint X=-10.1571 Y=-16 Z=0
    g39: Circle CenterX=-12.8401 CenterY=-17.6958 CenterZ=0 NormalX=0 NormalY=0 NormalZ=1 AngleXU=0 Radius=1
    g40: Circle CenterX=-13.3521 CenterY=-17.9027 CenterZ=0 NormalX=0 NormalY=0 NormalZ=1 AngleXU=0 Radius=1
    g41: Circle CenterX=-14 CenterY=-18 CenterZ=0 NormalX=0 NormalY=0 NormalZ=1 AngleXU=0 Radius=1
    g42: BSplineCurve PolesCount=3 KnotsCount=2 Degree=2 IsPeriodic=0
    g43: GeomPoint X=-12.8401 Y=-17.6958 Z=0
    g44: GeomPoint X=-14 Y=-18 Z=0
    g45: LineSegment StartX=-6.2 StartY=0 StartZ=0 EndX=-7.2 EndY=0 EndZ=0
    g46: LineSegment StartX=-7.2 StartY=0 StartZ=0 EndX=-7.2 EndY=-2 EndZ=0
    g47: LineSegment StartX=-7.2 StartY=-2 StartZ=0 EndX=-6.2215 EndY=-2 EndZ=0
    g48: LineSegment StartX=-6.32538 StartY=-4 StartZ=0 EndX=-7.65538 EndY=-4 EndZ=0
    g49: LineSegment StartX=-7.65538 StartY=-4 StartZ=0 EndX=-7.65538 EndY=-5.99526 EndZ=0
    g50: LineSegment StartX=-7.65538 StartY=-5.99526 StartZ=0 EndX=-6.48644 EndY=-5.99526 EndZ=0
    g51: LineSegment StartX=-6.77343 StartY=-8 StartZ=0 EndX=-8.43343 EndY=-8 EndZ=0
    g52: LineSegment StartX=-8.43343 StartY=-8 StartZ=0 EndX=-8.43343 EndY=-10 EndZ=0
    g53: LineSegment StartX=-8.43343 StartY=-10 StartZ=0 EndX=-7.19003 EndY=-10 EndZ=0
  constraints (112):
    c: Horizontal(g0)
    c: Distance(g0) = 2
    c: Block(g0)
    c: Vertical(g1)
    c: Coincident(g2,g0)
    c: Vertical(g2)
    c: Block(g2)
    c: Coincident(g6,g2)
    c: Weight(g3) = 1
    c: Equal(g3,g4)
    c: Equal(g3,g5)
    c: InternalAlignment(g3,g6)
    c: InternalAlignment(g4,g6)
    c: InternalAlignment(g5,g6)
    c: InternalAlignment(g7,g6)
    c: InternalAlignment(g8,g6)
    c: Block(g6)
    c: Coincident(g9,g1)
    c: Coincident(g9,g6)
    c: Horizontal(g9)
    c: Vertical(g10)
    c: Block(g10)
    c: Horizontal(g11)
    c: Block(g11)
    c: Coincident(g12,g10)
    c: Horizontal(g12)
    c: Block(g12)
    c: Coincident(g13,g11)
    c: Vertical(g13)
    c: Block(g13)
    c: Coincident(g14,g10)
    c: Horizontal(g14)
    c: Block(g14)
    c: Block(g9)
    c: Block(g1)
    c: Weight(g15) = 1
    c: Equal(g15,g16)
    c: Equal(g15,g17)
    c: InternalAlignment(g15,g18)
    c: InternalAlignment(g16,g18)
    c: InternalAlignment(g17,g18)
    c: InternalAlignment(g19,g18)
    c: InternalAlignment(g20,g18)
    c: Weight(g21) = 1
    c: Equal(g21,g22)
    c: Equal(g21,g23)
    c: InternalAlignment(g21,g24)
    c: InternalAlignment(g22,g24)
    c: InternalAlignment(g23,g24)
    c: InternalAlignment(g25,g24)
    c: InternalAlignment(g26,g24)
    c: Weight(g27) = 1
    c: Equal(g27,g28)
    c: Equal(g27,g29)
    c: Coincident(g30,g14)
    c: InternalAlignment(g27,g30)
    c: InternalAlignment(g28,g30)
    c: InternalAlignment(g29,g30)
    c: InternalAlignment(g31,g30)
    c: InternalAlignment(g32,g30)
    c: Coincident(g36,g12)
    c: Weight(g33) = 1
    c: Equal(g33,g34)
    c: Equal(g33,g35)
    c: Coincident(g36,g11)
    c: InternalAlignment(g33,g36)
    c: InternalAlignment(g34,g36)
    c: InternalAlignment(g35,g36)
    c: InternalAlignment(g37,g36)
    c: InternalAlignment(g38,g36)
    c: Coincident(g42,g13)
    c: Weight(g39) = 1
    c: Equal(g39,g40)
    c: Equal(g39,g41)
    c: Coincident(g42,g1)
    c: InternalAlignment(g39,g42)
    c: InternalAlignment(g40,g42)
    c: InternalAlignment(g41,g42)
    c: InternalAlignment(g43,g42)
    c: InternalAlignment(g44,g42)
    c: Block(g18)
    c: Block(g24)
    c: Block(g30)
    c: Block(g36)
    c: Block(g42)
    c: Horizontal(g45)
    c: Coincident(g45,g0)
    c: Vertical(g46)
    c: Coincident(g46,g45)
    c: Coincident(g47,g46)
    c: Coincident(g47,g18)
    c: Horizontal(g47)
    c: Block(g46)
    c: Coincident(g48,g18)
    c: Horizontal(g48)
    c: Distance(g48) = 1.33
    c: Vertical(g49)
    c: Coincident(g49,g48)
    c: Coincident(g50,g49)
    c: Coincident(g50,g24)
    c: Horizontal(g50)
    c: Tangent(g50,g22)
    c: Horizontal(g51)
    c: Coincident(g51,g24)
    c: Block(g51)
    c: Vertical(g52)
    c: Block(g52)
    c: Coincident(g52,g51)
    c: Coincident(g53,g52)
    c: Coincident(g53,g30)
    c: Horizontal(g53)
    c: Distance(g1) = 8.5
FEATURE [Part::Feature] Face024
  shape: bbox 9.8 x 26.5 x 2e-07 mm, 1 faces, 0 solids (baked)
FEATURE [Part::Revolution] Revolve024
  Angle = 360
  Axis = (0,1,0)
  Base = (0,0,0)
  FaceMakerClass = Part::FaceMakerBullseye
  Placement = pos=(0,0,0) rot=(0,0,1;1.5708rad)
  Solid = false
  Source = -> Face024
  Symmetric = false
FEATURE [Part::Feature] Face025
  shape: bbox 9.8 x 26.5 x 2e-07 mm, 1 faces, 0 solids (baked)
FEATURE [Part::Revolution] Revolve025
  Angle = 360
  Axis = (0,1,0)
  Base = (0,0,0)
  FaceMakerClass = Part::FaceMakerBullseye
  Placement = pos=(0,0,0) rot=(0,0,1;1.5708rad)
  Solid = false
  Source = -> Face025
  Symmetric = false
FEATURE [Part::MultiFuse] Fusion033
  Placement = pos=(-18,19,36) rot=(0,0,1;0rad)
  Shapes = -> [Revolve025,Revolve024]
FEATURE [Part::Cylinder] Cylinder014
  Angle = 360
  AttacherType = Attacher::AttachEngine3D
  Height = 20
  Placement = pos=(0,0,36.15) rot=(0,0,1;0rad)
  Radius = 14.3
FEATURE [Part::Cylinder] Cylinder015
  Angle = 360
  AttacherType = Attacher::AttachEngine3D
  Height = 10
  Placement = pos=(0,0,36.15) rot=(0,0,1;0rad)
  Radius = 4
FEATURE [Part::MultiFuse] Fusion034  label="removeToCreteHoleForPlugHousing004"
  Placement = pos=(-42,19,36) rot=(0,1,0;1.5708rad)
  Shapes = -> [Cylinder014,Cylinder015]
FEATURE [Part::Cut] Cut008  label="top004"
  Base = -> Cut004
  Placement = pos=(-1,0,0) rot=(0,0,1;0rad)
  Tool = -> Fusion034
FEATURE [Part::Box] Box005  label="Cube005"
  AttacherType = Attacher::AttachEngine3D
  Height = 28
  Length = 3
  Placement = pos=(110.7,19,22) rot=(0,0,1;0rad)
  Width = 15.7
FEATURE [Part::Cylinder] Cylinder016
  Angle = 360
  AttacherType = Attacher::AttachEngine3D
  Height = 10
  Placement = pos=(0,0,36.15) rot=(0,0,1;0rad)
  Radius = 4
FEATURE [Part::Cylinder] Cylinder017
  Angle = 360
  AttacherType = Attacher::AttachEngine3D
  Height = 20
  Placement = pos=(0,0,36.15) rot=(0,0,1;0rad)
  Radius = 10.3
FEATURE [Part::MultiFuse] Fusion035  label="removeToCreteHoleForPlugHousing005"
  Placement = pos=(70,19,36) rot=(0,1,0;1.5708rad)
  Shapes = -> [Cylinder017,Cylinder016]
FEATURE [Part::Cut] Cut009  label="plugHousingTab001"
  Base = -> Box005
  Placement = pos=(-107.4,-14,0) rot=(0,0,1;0rad)
  Tool = -> Fusion035
FEATURE [Part::Box] Box006  label="Cube006"
  AttacherType = Attacher::AttachEngine3D
  Height = 28
  Length = 3
  Placement = pos=(110.7,19,22) rot=(0,0,1;0rad)
  Width = 15.7
FEATURE [Part::Cylinder] Cylinder018
  Angle = 360
  AttacherType = Attacher::AttachEngine3D
  Height = 10
  Placement = pos=(0,0,36.15) rot=(0,0,1;0rad)
  Radius = 4
FEATURE [Part::Cylinder] Cylinder019
  Angle = 360
  AttacherType = Attacher::AttachEngine3D
  Height = 20
  Placement = pos=(0,0,36.15) rot=(0,0,1;0rad)
  Radius = 10.3
FEATURE [Part::MultiFuse] Fusion036  label="removeToCreteHoleForPlugHousing006"
  Placement = pos=(70,19,36) rot=(0,1,0;1.5708rad)
  Shapes = -> [Cylinder019,Cylinder018]
FEATURE [Part::Cut] Cut010  label="plugHousingTab002"
  Base = -> Box006
  Placement = pos=(-107.4,-14,0) rot=(0,0,1;0rad)
  Tool = -> Fusion036
FEATURE [Part::MultiFuse] Fusion037
  Placement = pos=(9.6,23,0) rot=(0,0,1;3.14159rad)
  Shapes = -> [Cut009,Cut010]
FEATURE [Part::Box] Box  label="Cube"
  AttacherType = Attacher::AttachEngine3D
  Height = 10
  Length = 3
  Placement = pos=(3.3,4,12) rot=(0,0,1;0rad)
  Width = 10
FEATURE [Part::Fillet] Fillet004
  Base = -> Fusion028
  Edges = 1 edges r=2: [Edge25]
FEATURE [Part::Fillet] Fillet005  label="plugHousing046"
  Base = -> Fillet004
  Edges = 1 edges r=2: [Edge8]
FEATURE [Part::Fillet] Fillet006
  Base = -> Box
  Edges = 1 edges r=2: [Edge11]
FEATURE [Part::Box] Box007  label="Cube007"
  AttacherType = Attacher::AttachEngine3D
  Height = 10
  Length = 3
  Placement = pos=(3.3,4,50) rot=(0,0,1;0rad)
  Width = 10
FEATURE [Part::Fillet] Fillet007
  Base = -> Box007
  Edges = 1 edges r=2: [Edge12]
FEATURE [Part::Box] Box008  label="Cube008"
  AttacherType = Attacher::AttachEngine3D
  Height = 28
  Length = 4
  Placement = pos=(5,0,22) rot=(0,0,1;0rad)
  Width = 10
FEATURE [Part::Fillet] Fillet008
  Base = -> Box008
  Edges = 1 edges r=1: [Edge7]
FEATURE [Part::Fillet] Fillet009
  Base = -> Fillet008
  Edges = 1 edges r=2: [Edge5]
FEATURE [Part::Fillet] Fillet010
  Base = -> Fillet009
  Edges = 1 edges r=2: [Edge2]
FEATURE [Sketcher::SketchObject] Sketch009  label="topSketch003"
  FullyConstrained = true
  sketch-geometry (4):
    g0: LineSegment StartX=16.8446 StartY=31.512 StartZ=0 EndX=16.3251 EndY=34.4666 EndZ=0
    g1: ArcOfCircle CenterX=19 CenterY=19.2524 CenterZ=0 NormalX=0 NormalY=0 NormalZ=1 AngleXU=0 Radius=15.4476 StartAngle=1.74483 EndAngle=2.72717
    g2: ArcOfCircle CenterX=19 CenterY=19.2524 CenterZ=0 NormalX=0 NormalY=0 NormalZ=1 AngleXU=0 Radius=12.4476 StartAngle=1.74483 EndAngle=2.73189
    g3: LineSegment StartX=4.86004 StartY=25.4725 StartZ=0 EndX=7.58253 EndY=24.2107 EndZ=0
  constraints (7):
    c: Block(g0)
    c: Coincident(g1,g0)
    c: Coincident(g2,g0)
    c: Coincident(g3,g1)
    c: Coincident(g3,g2)
    c: Block(g1)
    c: Block(g2)
FEATURE [Part::Extrusion] Extrude008
  Base = -> Sketch009
  Dir = (0,0,1)
  DirMode = 2
  FaceMakerClass = Part::FaceMakerBullseye
  LengthFwd = 10
  LengthRev = 0
  Placement = pos=(0,0,31) rot=(0,0,1;0rad)
  Solid = true
  Symmetric = false
FEATURE [Part::Cylinder] Cylinder020
  Angle = 360
  AttacherType = Attacher::AttachEngine3D
  Height = 20
  Placement = pos=(0,0,36.15) rot=(0,0,1;0rad)
  Radius = 8.2
FEATURE [Part::Cylinder] Cylinder021
  Angle = 360
  AttacherType = Attacher::AttachEngine3D
  Height = 10
  Placement = pos=(0,0,36.15) rot=(0,0,1;0rad)
  Radius = 4
FEATURE [Part::MultiFuse] Fusion038  label="removeToCreteHoleForPlugHousing007"
  Placement = pos=(-42,19,36) rot=(0,1,0;1.5708rad)
  Shapes = -> [Cylinder020,Cylinder021]
FEATURE [Part::Cut] Cut011
  Base = -> Extrude008
  Tool = -> Fusion038
FEATURE [Part::Fillet] Fillet011
  Base = -> Cut011
  Edges = 1 edges r=2: [Edge1]
FEATURE [Part::Fillet] Fillet012
  Base = -> Fillet011
  Edges = 1 edges r=2.5: [Edge1]
FEATURE [Part::Fillet] Fillet013
  Base = -> Fillet012
  Edges = 1 edges r=2.5: [Edge2]
FEATURE [Part::Box] Box010  label="Cube010"
  AttacherType = Attacher::AttachEngine3D
  Height = 16
  Length = 8
  Placement = pos=(12.7,31.52,28) rot=(0,0,1;0rad)
  Width = 4
FEATURE [Sketcher::SketchObject] Sketch010  label="topSketch004"
  FullyConstrained = true
  sketch-geometry (4):
    g0: LineSegment StartX=16.8446 StartY=31.512 StartZ=0 EndX=16.3251 EndY=34.4666 EndZ=0
    g1: ArcOfCircle CenterX=19 CenterY=19.2524 CenterZ=0 NormalX=0 NormalY=0 NormalZ=1 AngleXU=0 Radius=15.4476 StartAngle=1.74483 EndAngle=2.72717
    g2: ArcOfCircle CenterX=19 CenterY=19.2524 CenterZ=0 NormalX=0 NormalY=0 NormalZ=1 AngleXU=0 Radius=12.4476 StartAngle=1.74483 EndAngle=2.73189
    g3: LineSegment StartX=4.86004 StartY=25.4725 StartZ=0 EndX=7.58253 EndY=24.2107 EndZ=0
  constraints (7):
    c: Block(g0)
    c: Coincident(g1,g0)
    c: Coincident(g2,g0)
    c: Coincident(g3,g1)
    c: Coincident(g3,g2)
    c: Block(g1)
    c: Block(g2)
FEATURE [Part::Cylinder] Cylinder022
  Angle = 360
  AttacherType = Attacher::AttachEngine3D
  Height = 10
  Placement = pos=(0,0,36.15) rot=(0,0,1;0rad)
  Radius = 4
FEATURE [Sketcher::SketchObject] Sketch011  label="topSketch005"
  FullyConstrained = true
  sketch-geometry (4):
    g0: LineSegment StartX=16.8446 StartY=31.512 StartZ=0 EndX=16.3251 EndY=34.4666 EndZ=0
    g1: ArcOfCircle CenterX=19 CenterY=19.2524 CenterZ=0 NormalX=0 NormalY=0 NormalZ=1 AngleXU=0 Radius=15.4476 StartAngle=1.74483 EndAngle=2.72717
    g2: ArcOfCircle CenterX=19 CenterY=19.2524 CenterZ=0 NormalX=0 NormalY=0 NormalZ=1 AngleXU=0 Radius=12.4476 StartAngle=1.74483 EndAngle=2.73189
    g3: LineSegment StartX=4.86004 StartY=25.4725 StartZ=0 EndX=7.58253 EndY=24.2107 EndZ=0
  constraints (7):
    c: Block(g0)
    c: Coincident(g1,g0)
    c: Coincident(g2,g0)
    c: Coincident(g3,g1)
    c: Coincident(g3,g2)
    c: Block(g1)
    c: Block(g2)
FEATURE [Part::Extrusion] Extrude010
  Base = -> Sketch011
  Dir = (0,0,1)
  DirMode = 2
  FaceMakerClass = Part::FaceMakerBullseye
  LengthFwd = 10.6
  LengthRev = 0
  Placement = pos=(0,0,31) rot=(0,0,1;0rad)
  Solid = true
  Symmetric = false
FEATURE [Part::Cylinder] Cylinder023
  Angle = 360
  AttacherType = Attacher::AttachEngine3D
  Height = 20
  Placement = pos=(0,0,36.15) rot=(0,0,1;0rad)
  Radius = 8.2
FEATURE [Part::MultiFuse] Fusion039  label="removeToCreteHoleForPlugHousing008"
  Placement = pos=(-42,19,36) rot=(0,1,0;1.5708rad)
  Shapes = -> [Cylinder023,Cylinder022]
FEATURE [Part::Cut] Cut012
  Base = -> Extrude010
  Placement = pos=(0,0,-0.3) rot=(0,0,1;0rad)
  Tool = -> Fusion039
FEATURE [Part::Cut] Cut013
  Base = -> Box010
  Tool = -> Cut012
FEATURE [Part::Fillet] Fillet014
  Base = -> Cut013
  Edges = 1 edges r=0.7: [Edge13]
FEATURE [Part::Fillet] Fillet015
  Base = -> Fillet014
  Edges = 1 edges r=0.7: [Edge13]
FEATURE [Part::Fillet] Fillet016
  Base = -> Fillet015
  Edges = 1 edges r=0.7: [Edge16]
FEATURE [Part::Fillet] Fillet017
  Base = -> Fillet016
  Edges = 1 edges r=0.7: [Edge11]
FEATURE [Part::Fillet] Fillet018
  Base = -> Fillet017
  Edges = 1 edges r=0.7: [Edge10]
FEATURE [Part::Fillet] Fillet019
  Base = -> Fillet018
  Edges = 1 edges r=1.2: [Edge5]
FEATURE [Part::Fillet] Fillet020
  Base = -> Fillet019
  Edges = 1 edges r=1.2: [Edge12]
FEATURE [Part::Fillet] Fillet021
  Base = -> Fillet020
  Edges = 1 edges r=2: [Edge1]
  Placement = pos=(0.3,0,0) rot=(0,0,1;0rad)
FEATURE [Part::MultiFuse] Fusion040  label="top005"
  Shapes = -> [Cut008,Fillet021]
FEATURE [Part::MultiFuse] Fusion041  label="wireHolder"
  Shapes = -> [Fusion033,Fillet013]
FEATURE [Part::MultiFuse] Fusion042
  Shapes = -> [Fillet007,Fusion041]
FEATURE [Part::MultiFuse] Fusion043  label="wireHolder001"
  Shapes = -> [Fusion042,Fillet010]
FEATURE [Part::MultiFuse] Fusion044  label="wireHolder002"
  Shapes = -> [Fillet006,Fusion037,Fusion043]
FEATURE [Part::Feature] Face026
  shape: bbox 11 x 6 x 2e-07 mm, 1 faces, 0 solids (baked)
FEATURE [Part::Revolution] Revolve026
  Angle = 360
  Axis = (0,1,0)
  Base = (0,0,0)
  FaceMakerClass = Part::FaceMakerBullseye
  Placement = pos=(30.3,-1,19.7) rot=(0,0,1;0rad)
  Solid = false
  Source = -> Face026
  Symmetric = false
FEATURE [Sketcher::SketchObject] Sketch013  label="topSketch006"
  FullyConstrained = true
  sketch-geometry (13):
    g0: LineSegment StartX=117 StartY=19 StartZ=0 EndX=117 EndY=38 EndZ=0
    g1: ArcOfCircle CenterX=98 CenterY=19 CenterZ=0 NormalX=0 NormalY=0 NormalZ=1 AngleXU=0 Radius=19 StartAngle=5.7297 EndAngle=6.28319
    g2: LineSegment StartX=0 StartY=3 StartZ=0 EndX=0 EndY=19 EndZ=0
    g3: LineSegment StartX=19 StartY=38 StartZ=0 EndX=117 EndY=38 EndZ=0
    g4: ArcOfCircle CenterX=19 CenterY=19 CenterZ=0 NormalX=0 NormalY=0 NormalZ=1 AngleXU=0 Radius=19 StartAngle=1.5708 EndAngle=3.14159
    g5: ArcOfCircle CenterX=19 CenterY=19 CenterZ=0 NormalX=0 NormalY=0 NormalZ=1 AngleXU=0 Radius=16 StartAngle=1.5708 EndAngle=3.14159
    g6: ArcOfCircle CenterX=98 CenterY=19 CenterZ=0 NormalX=0 NormalY=0 NormalZ=1 AngleXU=0 Radius=16 StartAngle=5.60905 EndAngle=6.28319
    g7: LineSegment StartX=114 StartY=19 StartZ=0 EndX=114 EndY=35 EndZ=0
    g8: LineSegment StartX=110.5 StartY=9.01251 StartZ=0 EndX=114.163 EndY=9.01251 EndZ=0
    g9: LineSegment StartX=114 StartY=35 StartZ=0 EndX=19 EndY=35 EndZ=0
    g10: LineSegment StartX=0 StartY=3 StartZ=0 EndX=0 EndY=0 EndZ=0
    g11: LineSegment StartX=3 StartY=0 StartZ=0 EndX=0 EndY=0 EndZ=0
    g12: LineSegment StartX=3 StartY=19 StartZ=0 EndX=3 EndY=0 EndZ=0
  constraints (33):
    c: Vertical(g0)
    c: Distance(g0) = 19
    c: Block(g0)
    c: Coincident(g1,g0)
    c: Block(g1)
    c: Vertical(g2)
    c: Block(g2)
    c: Coincident(g3,g0)
    c: Horizontal(g3)
    c: Distance(g3) = 98
    c: Coincident(g4,g3)
    c: Coincident(g4,g2)
    c: Block(g4)
    c: Coincident(g5,g4)
    c: Coincident(g6,g1)
    c: Block(g6)
    c: Block(g5)
    c: Coincident(g7,g6)
    c: Vertical(g7)
    c: Coincident(g8,g6)
    c: Coincident(g8,g1)
    c: Coincident(g9,g7)
    c: Coincident(g9,g5)
    c: Horizontal(g9)
    c: Tangent(g9,g5)
    c: Coincident(g10,g2)
    c: Distance(g10) = 3
    c: Vertical(g10)
    c: Coincident(g11,g10)
    c: Horizontal(g11)
    c: Coincident(g12,g5)
    c: Coincident(g12,g11)
    c: Vertical(g12)
FEATURE [Part::Extrusion] Extrude011  label="top006"
  Base = -> Sketch013
  Dir = (0,0,1)
  DirMode = 2
  FaceMakerClass = Part::FaceMakerBullseye
  LengthFwd = 72
  LengthRev = 0
  Solid = true
  Symmetric = false
FEATURE [Sketcher::SketchObject] Sketch014
  FullyConstrained = true
  MapMode = 3
  Placement = pos=(0,0,0) rot=(1,0,0;1.5708rad)
  Support = -> [Extrude011]
  sketch-geometry (8):
    g0: Circle CenterX=80.351 CenterY=-67.6202 CenterZ=0 NormalX=0 NormalY=0 NormalZ=1 AngleXU=0 Radius=2
    g1: Circle CenterX=80.351 CenterY=-67.6202 CenterZ=0 NormalX=0 NormalY=0 NormalZ=1 AngleXU=0 Radius=3
    g2: Circle CenterX=80.351 CenterY=-4.92017 CenterZ=0 NormalX=0 NormalY=0 NormalZ=1 AngleXU=0 Radius=2
    g3: Circle CenterX=80.351 CenterY=-4.92017 CenterZ=0 NormalX=0 NormalY=0 NormalZ=1 AngleXU=0 Radius=3
    g4: Circle CenterX=23.851 CenterY=-4.92017 CenterZ=0 NormalX=0 NormalY=0 NormalZ=1 AngleXU=0 Radius=2
    g5: Circle CenterX=23.851 CenterY=-4.92017 CenterZ=0 NormalX=0 NormalY=0 NormalZ=1 AngleXU=0 Radius=3
    g6: Circle CenterX=23.851 CenterY=-67.6202 CenterZ=0 NormalX=0 NormalY=0 NormalZ=1 AngleXU=0 Radius=2
    g7: Circle CenterX=23.851 CenterY=-67.6202 CenterZ=0 NormalX=0 NormalY=0 NormalZ=1 AngleXU=0 Radius=3
  constraints (8):
    c: Block(g3)
    c: Block(g2)
    c: Block(g1)
    c: Block(g0)
    c: Block(g6)
    c: Block(g7)
    c: Block(g4)
    c: Block(g5)
FEATURE [Part::Feature] Face027
  shape: bbox 11 x 6 x 2e-07 mm, 1 faces, 0 solids (baked)
FEATURE [Part::Revolution] Revolve027
  Angle = 360
  Axis = (0,1,0)
  Base = (0,0,0)
  FaceMakerClass = Part::FaceMakerBullseye
  Placement = pos=(30.3,-1,51.7) rot=(0,0,1;0rad)
  Solid = false
  Source = -> Face027
  Symmetric = false
FEATURE [Part::Feature] Face028
  shape: bbox 11 x 6 x 2e-07 mm, 1 faces, 0 solids (baked)
FEATURE [Part::Revolution] Revolve028
  Angle = 360
  Axis = (0,1,0)
  Base = (0,0,0)
  FaceMakerClass = Part::FaceMakerBullseye
  Placement = pos=(62.3,-1,19.7) rot=(0,0,1;0rad)
  Solid = false
  Source = -> Face028
  Symmetric = false
FEATURE [Part::Feature] Face029
  shape: bbox 11 x 6 x 2e-07 mm, 1 faces, 0 solids (baked)
FEATURE [Part::Revolution] Revolve029
  Angle = 360
  Axis = (0,1,0)
  Base = (0,0,0)
  FaceMakerClass = Part::FaceMakerBullseye
  Placement = pos=(62.3,-1,51.7) rot=(0,0,1;0rad)
  Solid = false
  Source = -> Face029
  Symmetric = false
FEATURE [Part::Feature] Wire
  shape: bbox 11 x 5.2 x 2e-07 mm, 0 faces, 0 solids (baked)
FEATURE [Part::Revolution] Revolve030
  Angle = 360
  Axis = (0,1,0)
  Base = (0,0,0)
  FaceMakerClass = Part::FaceMakerBullseye
  Placement = pos=(30.3,38,19.7) rot=(0,0,1;0rad)
  Solid = true
  Source = -> Wire
  Symmetric = false
FEATURE [Part::Feature] Wire001
  shape: bbox 11 x 5.2 x 2e-07 mm, 0 faces, 0 solids (baked)
FEATURE [Part::Revolution] Revolve031
  Angle = 360
  Axis = (0,1,0)
  Base = (0,0,0)
  FaceMakerClass = Part::FaceMakerBullseye
  Placement = pos=(30.3,38,51.7) rot=(0,0,1;0rad)
  Solid = true
  Source = -> Wire001
  Symmetric = false
FEATURE [Part::Feature] Wire002
  shape: bbox 11 x 5.2 x 2e-07 mm, 0 faces, 0 solids (baked)
FEATURE [Part::Revolution] Revolve032
  Angle = 360
  Axis = (0,1,0)
  Base = (0,0,0)
  FaceMakerClass = Part::FaceMakerBullseye
  Placement = pos=(62.3,38,51.7) rot=(0,0,1;0rad)
  Solid = true
  Source = -> Wire002
  Symmetric = false
FEATURE [Part::Feature] Wire003
  shape: bbox 11 x 5.2 x 2e-07 mm, 0 faces, 0 solids (baked)
FEATURE [Part::Revolution] Revolve033
  Angle = 360
  Axis = (0,1,0)
  Base = (0,0,0)
  FaceMakerClass = Part::FaceMakerBullseye
  Placement = pos=(62.3,38,19.7) rot=(0,0,1;0rad)
  Solid = true
  Source = -> Wire003
  Symmetric = false
FEATURE [Part::MultiFuse] Fusion045  label="altRandScrewHousing"
  Shapes = -> [Revolve029,Revolve027,Revolve028,Revolve026]
FEATURE [Part::MultiFuse] Fusion046  label="fanScrewHousing"
  Shapes = -> [Revolve033,Revolve032,Revolve031,Revolve030]
FEATURE [Sketcher::SketchObject] Sketch015
  FullyConstrained = true
  sketch-geometry (17):
    g0: Circle CenterX=-3.5 CenterY=23.5 CenterZ=0 NormalX=0 NormalY=0 NormalZ=1 AngleXU=0 Radius=1
    g1: Circle CenterX=-1 CenterY=15.25 CenterZ=0 NormalX=0 NormalY=0 NormalZ=1 AngleXU=0 Radius=1
    g2: Circle CenterX=-3.5 CenterY=7 CenterZ=0 NormalX=0 NormalY=0 NormalZ=1 AngleXU=0 Radius=1
    g3: BSplineCurve PolesCount=3 KnotsCount=2 Degree=2 IsPeriodic=0
    g4: GeomPoint X=-3.5 Y=23.5 Z=0
    g5: GeomPoint X=-3.5 Y=7 Z=0
    g6: Circle CenterX=-4.8 CenterY=30.5 CenterZ=0 NormalX=0 NormalY=0 NormalZ=1 AngleXU=0 Radius=1
    g7: Circle CenterX=-3.5 CenterY=30.5 CenterZ=0 NormalX=0 NormalY=0 NormalZ=1 AngleXU=0 Radius=1
    g8: Circle CenterX=-3.5 CenterY=29.2 CenterZ=0 NormalX=0 NormalY=0 NormalZ=1 AngleXU=0 Radius=1
    g9: BSplineCurve PolesCount=3 KnotsCount=2 Degree=2 IsPeriodic=0
    g10: GeomPoint X=-4.8 Y=30.5 Z=0
    g11: GeomPoint X=-3.5 Y=29.2 Z=0
    g12: LineSegment StartX=-3.5 StartY=29.2 StartZ=0 EndX=-3.5 EndY=23.5 EndZ=0
    g13: LineSegment StartX=-4.8 StartY=30.5 StartZ=0 EndX=0 EndY=30.5 EndZ=0
    g14: LineSegment StartX=-3.5 StartY=0.3 StartZ=0 EndX=0 EndY=0.3 EndZ=0
    g15: LineSegment StartX=-3.5 StartY=0.3 StartZ=0 EndX=-3.5 EndY=7 EndZ=0
    g16: LineSegment StartX=0 StartY=0.3 StartZ=0 EndX=0 EndY=30.5 EndZ=0
  constraints (33):
    c: Weight(g0) = 1
    c: Equal(g0,g1)
    c: Equal(g0,g2)
    c: InternalAlignment(g0,g3)
    c: InternalAlignment(g1,g3)
    c: InternalAlignment(g2,g3)
    c: InternalAlignment(g4,g3)
    c: InternalAlignment(g5,g3)
    c: Block(g3)
    c: Weight(g6) = 1
    c: Equal(g6,g7)
    c: Equal(g6,g8)
    c: InternalAlignment(g6,g9)
    c: InternalAlignment(g7,g9)
    c: InternalAlignment(g8,g9)
    c: InternalAlignment(g10,g9)
    c: InternalAlignment(g11,g9)
    c: Block(g9)
    c: Coincident(g12,g9)
    c: Coincident(g12,g3)
    c: Vertical(g12)
    c: Coincident(g13,g9)
    c: Horizontal(g13)
    c: Distance(g13) = 4.8
    c: Horizontal(g14)
    c: Block(g14)
    c: Coincident(g15,g14)
    c: Coincident(g15,g3)
    c: Vertical(g15)
    c: Coincident(g16,g14)
    c: Coincident(g16,g13)
    c: Vertical(g16)
    c: Tangent(g16,g1)
FEATURE [Sketcher::SketchObject] Sketch016
  FullyConstrained = true
  sketch-geometry (16):
    g0: Circle CenterX=-3.5 CenterY=23.5 CenterZ=0 NormalX=0 NormalY=0 NormalZ=1 AngleXU=0 Radius=1
    g1: Circle CenterX=-1 CenterY=15.25 CenterZ=0 NormalX=0 NormalY=0 NormalZ=1 AngleXU=0 Radius=1
    g2: Circle CenterX=-3.5 CenterY=7 CenterZ=0 NormalX=0 NormalY=0 NormalZ=1 AngleXU=0 Radius=1
    g3: BSplineCurve PolesCount=3 KnotsCount=2 Degree=2 IsPeriodic=0
    g4: GeomPoint X=-3.5 Y=23.5 Z=0
    g5: GeomPoint X=-3.5 Y=7 Z=0
    g6: LineSegment StartX=-3.5 StartY=28.2 StartZ=0 EndX=-3.5 EndY=23.5 EndZ=0
    g7: LineSegment StartX=0 StartY=29.5 StartZ=0 EndX=0 EndY=30 EndZ=0
    g8: LineSegment StartX=-3.5 StartY=28.2 StartZ=0 EndX=-3.5 EndY=30 EndZ=0
    g9: LineSegment StartX=0 StartY=30 StartZ=0 EndX=0 EndY=30.5 EndZ=0
    g10: LineSegment StartX=0 StartY=30.5 StartZ=0 EndX=-3.5 EndY=30.5 EndZ=0
    g11: LineSegment StartX=-3.5 StartY=30.5 StartZ=0 EndX=-3.5 EndY=30 EndZ=0
    g12: LineSegment StartX=0 StartY=29.5 StartZ=0 EndX=0 EndY=5 EndZ=0
    g13: LineSegment StartX=-3.5 StartY=0.3 StartZ=0 EndX=-3.5 EndY=7 EndZ=0
    g14: LineSegment StartX=-3.5 StartY=0.3 StartZ=0 EndX=0 EndY=0.3 EndZ=0
    g15: LineSegment StartX=0 StartY=5 StartZ=0 EndX=0 EndY=0.3 EndZ=0
  constraints (39):
    c: Weight(g0) = 1
    c: Equal(g0,g1)
    c: Equal(g0,g2)
    c: InternalAlignment(g0,g3)
    c: InternalAlignment(g1,g3)
    c: InternalAlignment(g2,g3)
    c: InternalAlignment(g4,g3)
    c: InternalAlignment(g5,g3)
    c: Block(g3)
    c: Coincident(g6,g3)
    c: Vertical(g6)
    c: Vertical(g7)
    c: Distance(g7) = 0.5
    c: Coincident(g8,g6)
    c: Vertical(g8)
    c: Block(g6)
    c: Block(g7)
    c: Vertical(g9)
    c: Equal(g7,g9) = 0.5
    c: Block(g9)
    c: Coincident(g9,g7)
    c: Horizontal(g10)
    c: Coincident(g10,g9)
    c: Coincident(g11,g10)
    c: Coincident(g11,g8)
    c: Vertical(g11)
    c: Block(g11)
    c: Coincident(g12,g7)
    c: Vertical(g12)
    c: Coincident(g13,g3)
    c: Vertical(g13)
    c: Distance(g13) = 6.7
    c: Coincident(g14,g13)
    c: Horizontal(g14)
    c: Block(g14)
    c: Coincident(g15,g12)
    c: Coincident(g15,g14)
    c: Vertical(g15)
    c: Block(g15)
FEATURE [Sketcher::SketchObject] Sketch017
  FullyConstrained = true
  sketch-geometry (11):
    g0: LineSegment StartX=-3.5 StartY=1e-16 StartZ=0 EndX=-1.6 EndY=1e-16 EndZ=0
    g1: LineSegment StartX=-1.6 StartY=1e-16 StartZ=0 EndX=-1.6 EndY=1.5 EndZ=0
    g2: LineSegment StartX=-3.5 StartY=1.5 StartZ=0 EndX=-1.6 EndY=1.5 EndZ=0
    g3: LineSegment StartX=-3.5 StartY=1e-16 StartZ=0 EndX=-4.8 EndY=1e-16 EndZ=0
    g4: Circle CenterX=-3.5 CenterY=1.3 CenterZ=0 NormalX=0 NormalY=0 NormalZ=1 AngleXU=0 Radius=1
    g5: Circle CenterX=-3.5 CenterY=1e-16 CenterZ=0 NormalX=0 NormalY=0 NormalZ=1 AngleXU=0 Radius=1
    g6: Circle CenterX=-4.8 CenterY=1e-16 CenterZ=0 NormalX=0 NormalY=0 NormalZ=1 AngleXU=0 Radius=1
    g7: BSplineCurve PolesCount=3 KnotsCount=2 Degree=2 IsPeriodic=0
    g8: GeomPoint X=-3.5 Y=1.3 Z=0
    g9: GeomPoint X=-4.8 Y=1e-16 Z=0
    g10: LineSegment StartX=-3.5 StartY=1.3 StartZ=0 EndX=-3.5 EndY=1.5 EndZ=0
  constraints (24):
    c: Horizontal(g0)
    c: Distance(g0) = 1.9
    c: Block(g0)
    c: Coincident(g1,g0)
    c: Vertical(g1)
    c: Coincident(g2,g1)
    c: Horizontal(g2)
    c: Coincident(g3,g0)
    c: Horizontal(g3)
    c: Distance(g3) = 1.3
    c: Weight(g4) = 1
    c: Equal(g4,g5)
    c: Coincident(g5,g0)
    c: Equal(g4,g6)
    c: Coincident(g7,g3)
    c: InternalAlignment(g4,g7)
    c: InternalAlignment(g5,g7)
    c: InternalAlignment(g6,g7)
    c: InternalAlignment(g8,g7)
    c: InternalAlignment(g9,g7)
    c: Coincident(g10,g7)
    c: Coincident(g10,g2)
    c: Vertical(g10)
    c: Block(g10)
FEATURE [Part::Feature] Face035
  shape: bbox 3.2 x 1.5 x 2e-07 mm, 1 faces, 0 solids (baked)
FEATURE [Part::Revolution] Revolve039  label="backCaseScrewRetainer"
  Angle = 360
  Axis = (0,1,0)
  Base = (0,0,0)
  FaceMakerClass = Part::FaceMakerBullseye
  Placement = pos=(12.5,3,62) rot=(0,0,1;0rad)
  Solid = false
  Source = -> Face035
  Symmetric = false
FEATURE [Part::Feature] Face036
  shape: bbox 3.2 x 1.5 x 2e-07 mm, 1 faces, 0 solids (baked)
FEATURE [Part::Feature] Face039
  shape: bbox 4.8 x 30.2 x 2e-07 mm, 1 faces, 0 solids (baked)
FEATURE [Part::Revolution] Revolve043  label="frontCaseScrewPost002"
  Angle = 360
  Axis = (0,1,0)
  Base = (0,0,0)
  FaceMakerClass = Part::FaceMakerBullseye
  Placement = pos=(89.5,4.5,3.5) rot=(0,0,1;0rad)
  Solid = false
  Source = -> Face039
  Symmetric = false
FEATURE [Part::Feature] Face042
  shape: bbox 4.8 x 30.2 x 2e-07 mm, 1 faces, 0 solids (baked)
FEATURE [Part::Revolution] Revolve046  label="frontCaseScrewPost003"
  Angle = 360
  Axis = (0,1,0)
  Base = (0,0,0)
  FaceMakerClass = Part::FaceMakerBullseye
  Placement = pos=(89.5,4.5,68.5) rot=(0,0,1;0rad)
  Solid = false
  Source = -> Face042
  Symmetric = false
FEATURE [Part::Feature] Face043
  shape: bbox 3.2 x 1.5 x 2e-07 mm, 1 faces, 0 solids (baked)
FEATURE [Part::Revolution] Revolve047  label="frontCaseScrewRetainer002"
  Angle = 360
  Axis = (0,1,0)
  Base = (0,0,0)
  FaceMakerClass = Part::FaceMakerBullseye
  Placement = pos=(89.5,3,68.5) rot=(0,0,1;0rad)
  Solid = false
  Source = -> Face043
  Symmetric = false
FEATURE [Part::Feature] Face044
  shape: bbox 3.2 x 1.5 x 2e-07 mm, 1 faces, 0 solids (baked)
FEATURE [Part::Revolution] Revolve048  label="frontCaseScrewRetainer003"
  Angle = 360
  Axis = (0,1,0)
  Base = (0,0,0)
  FaceMakerClass = Part::FaceMakerBullseye
  Placement = pos=(89.5,3,3.5) rot=(0,0,1;0rad)
  Solid = false
  Source = -> Face044
  Symmetric = false
FEATURE [App::MeasureDistance] Distance002  label="Distance: 1.67 mm"
  Distance = 1.66921
  P1 = (99.2361,4.7524,71.7)
  P2 = (99.2347,6.42161,71.7)
FEATURE [Sketcher::SketchObject] Sketch018
  FullyConstrained = true
  sketch-geometry (7):
    g0: LineSegment StartX=0 StartY=0 StartZ=0 EndX=0 EndY=6 EndZ=0
    g1: Circle CenterX=0 CenterY=0 CenterZ=0 NormalX=0 NormalY=0 NormalZ=1 AngleXU=0 Radius=1
    g2: Circle CenterX=8 CenterY=6 CenterZ=0 NormalX=0 NormalY=0 NormalZ=1 AngleXU=0 Radius=1
    g3: BSplineCurve PolesCount=3 KnotsCount=2 Degree=2 IsPeriodic=0
    g4: GeomPoint X=0 Y=0 Z=0
    g5: GeomPoint X=8 Y=6 Z=0
    g6: LineSegment StartX=0 StartY=6 StartZ=0 EndX=8 EndY=6 EndZ=0
  constraints (14):
    c: Coincident(g0,g-1)
    c: Distance(g0) = 6
    c: Vertical(g0)
    c: Coincident(g3,g0)
    c: Weight(g1) = 1
    c: Equal(g1,g2)
    c: InternalAlignment(g1,g3)
    c: InternalAlignment(g2,g3)
    c: InternalAlignment(g4,g3)
    c: InternalAlignment(g5,g3)
    c: Block(g3)
    c: Coincident(g6,g0)
    c: Coincident(g6,g3)
    c: Horizontal(g6)
FEATURE [Part::Extrusion] Extrude012  label="caseScrewPillarBracket"
  Base = -> Sketch018
  Dir = (0,0,1)
  DirMode = 2
  FaceMakerClass = Part::FaceMakerBullseye
  LengthFwd = 2.4
  LengthRev = 0
  Placement = pos=(15.76,29,8.8) rot=(0,1,0;0rad)
  Solid = true
  Symmetric = false
FEATURE [Sketcher::SketchObject] Sketch019
  FullyConstrained = true
  sketch-geometry (7):
    g0: LineSegment StartX=0 StartY=0 StartZ=0 EndX=0 EndY=6 EndZ=0
    g1: Circle CenterX=0 CenterY=0 CenterZ=0 NormalX=0 NormalY=0 NormalZ=1 AngleXU=0 Radius=1
    g2: Circle CenterX=8 CenterY=6 CenterZ=0 NormalX=0 NormalY=0 NormalZ=1 AngleXU=0 Radius=1
    g3: BSplineCurve PolesCount=3 KnotsCount=2 Degree=2 IsPeriodic=0
    g4: GeomPoint X=0 Y=0 Z=0
    g5: GeomPoint X=8 Y=6 Z=0
    g6: LineSegment StartX=0 StartY=6 StartZ=0 EndX=8 EndY=6 EndZ=0
  constraints (14):
    c: Coincident(g0,g-1)
    c: Distance(g0) = 6
    c: Vertical(g0)
    c: Coincident(g3,g0)
    c: Weight(g1) = 1
    c: Equal(g1,g2)
    c: InternalAlignment(g1,g3)
    c: InternalAlignment(g2,g3)
    c: InternalAlignment(g4,g3)
    c: InternalAlignment(g5,g3)
    c: Block(g3)
    c: Coincident(g6,g0)
    c: Coincident(g6,g3)
    c: Horizontal(g6)
FEATURE [Part::Extrusion] Extrude013  label="caseScrewPillarBracket001"
  Base = -> Sketch019
  Dir = (0,0,1)
  DirMode = 2
  FaceMakerClass = Part::FaceMakerBullseye
  LengthFwd = 2.4
  LengthRev = 0
  Placement = pos=(15.76,29,60.8) rot=(0,0,1;0rad)
  Solid = true
  Symmetric = false
FEATURE [Sketcher::SketchObject] Sketch020
  FullyConstrained = true
  sketch-geometry (7):
    g0: LineSegment StartX=0 StartY=0 StartZ=0 EndX=0 EndY=6 EndZ=0
    g1: Circle CenterX=0 CenterY=0 CenterZ=0 NormalX=0 NormalY=0 NormalZ=1 AngleXU=0 Radius=1
    g2: Circle CenterX=8 CenterY=6 CenterZ=0 NormalX=0 NormalY=0 NormalZ=1 AngleXU=0 Radius=1
    g3: BSplineCurve PolesCount=3 KnotsCount=2 Degree=2 IsPeriodic=0
    g4: GeomPoint X=0 Y=0 Z=0
    g5: GeomPoint X=8 Y=6 Z=0
    g6: LineSegment StartX=0 StartY=6 StartZ=0 EndX=8 EndY=6 EndZ=0
  constraints (14):
    c: Coincident(g0,g-1)
    c: Distance(g0) = 6
    c: Vertical(g0)
    c: Coincident(g3,g0)
    c: Weight(g1) = 1
    c: Equal(g1,g2)
    c: InternalAlignment(g1,g3)
    c: InternalAlignment(g2,g3)
    c: InternalAlignment(g4,g3)
    c: InternalAlignment(g5,g3)
    c: Block(g3)
    c: Coincident(g6,g0)
    c: Coincident(g6,g3)
    c: Horizontal(g6)
FEATURE [Part::Extrusion] Extrude014  label="caseScrewPillarBracket002"
  Base = -> Sketch020
  Dir = (0,0,1)
  DirMode = 2
  FaceMakerClass = Part::FaceMakerBullseye
  LengthFwd = 2.4
  LengthRev = 0
  Placement = pos=(13.7,29,13.26) rot=(0,1,0;-1.5708rad)
  Solid = true
  Symmetric = false
FEATURE [Sketcher::SketchObject] Sketch021
  FullyConstrained = true
  sketch-geometry (7):
    g0: LineSegment StartX=0 StartY=0 StartZ=0 EndX=0 EndY=6 EndZ=0
    g1: Circle CenterX=0 CenterY=0 CenterZ=0 NormalX=0 NormalY=0 NormalZ=1 AngleXU=0 Radius=1
    g2: Circle CenterX=8 CenterY=6 CenterZ=0 NormalX=0 NormalY=0 NormalZ=1 AngleXU=0 Radius=1
    g3: BSplineCurve PolesCount=3 KnotsCount=2 Degree=2 IsPeriodic=0
    g4: GeomPoint X=0 Y=0 Z=0
    g5: GeomPoint X=8 Y=6 Z=0
    g6: LineSegment StartX=0 StartY=6 StartZ=0 EndX=8 EndY=6 EndZ=0
  constraints (14):
    c: Coincident(g0,g-1)
    c: Distance(g0) = 6
    c: Vertical(g0)
    c: Coincident(g3,g0)
    c: Weight(g1) = 1
    c: Equal(g1,g2)
    c: InternalAlignment(g1,g3)
    c: InternalAlignment(g2,g3)
    c: InternalAlignment(g4,g3)
    c: InternalAlignment(g5,g3)
    c: Block(g3)
    c: Coincident(g6,g0)
    c: Coincident(g6,g3)
    c: Horizontal(g6)
FEATURE [Part::Extrusion] Extrude015  label="caseScrewPillarBracket003"
  Base = -> Sketch021
  Dir = (0,0,1)
  DirMode = 2
  FaceMakerClass = Part::FaceMakerBullseye
  LengthFwd = 2.4
  LengthRev = 0
  Placement = pos=(11.3,29,58.74) rot=(0,1,0;1.5708rad)
  Solid = true
  Symmetric = false
FEATURE [Sketcher::SketchObject] Sketch022
  FullyConstrained = true
  sketch-geometry (7):
    g0: LineSegment StartX=0 StartY=0 StartZ=0 EndX=0 EndY=6 EndZ=0
    g1: Circle CenterX=0 CenterY=0 CenterZ=0 NormalX=0 NormalY=0 NormalZ=1 AngleXU=0 Radius=1
    g2: Circle CenterX=8 CenterY=6 CenterZ=0 NormalX=0 NormalY=0 NormalZ=1 AngleXU=0 Radius=1
    g3: BSplineCurve PolesCount=3 KnotsCount=2 Degree=2 IsPeriodic=0
    g4: GeomPoint X=0 Y=0 Z=0
    g5: GeomPoint X=8 Y=6 Z=0
    g6: LineSegment StartX=0 StartY=6 StartZ=0 EndX=8 EndY=6 EndZ=0
  constraints (14):
    c: Coincident(g0,g-1)
    c: Distance(g0) = 6
    c: Vertical(g0)
    c: Coincident(g3,g0)
    c: Weight(g1) = 1
    c: Equal(g1,g2)
    c: InternalAlignment(g1,g3)
    c: InternalAlignment(g2,g3)
    c: InternalAlignment(g4,g3)
    c: InternalAlignment(g5,g3)
    c: Block(g3)
    c: Coincident(g6,g0)
    c: Coincident(g6,g3)
    c: Horizontal(g6)
FEATURE [Part::Extrusion] Extrude016  label="caseScrewPillarBracket004"
  Base = -> Sketch022
  Dir = (0,0,1)
  DirMode = 2
  FaceMakerClass = Part::FaceMakerBullseye
  LengthFwd = 2.4
  LengthRev = 0
  Placement = pos=(88.3,29,65.23) rot=(0,1,0;1.5708rad)
  Solid = true
  Symmetric = false
FEATURE [Sketcher::SketchObject] Sketch023
  FullyConstrained = true
  sketch-geometry (7):
    g0: LineSegment StartX=0 StartY=0 StartZ=0 EndX=0 EndY=6 EndZ=0
    g1: Circle CenterX=0 CenterY=0 CenterZ=0 NormalX=0 NormalY=0 NormalZ=1 AngleXU=0 Radius=1
    g2: Circle CenterX=8 CenterY=6 CenterZ=0 NormalX=0 NormalY=0 NormalZ=1 AngleXU=0 Radius=1
    g3: BSplineCurve PolesCount=3 KnotsCount=2 Degree=2 IsPeriodic=0
    g4: GeomPoint X=0 Y=0 Z=0
    g5: GeomPoint X=8 Y=6 Z=0
    g6: LineSegment StartX=0 StartY=6 StartZ=0 EndX=8 EndY=6 EndZ=0
  constraints (14):
    c: Coincident(g0,g-1)
    c: Distance(g0) = 6
    c: Vertical(g0)
    c: Coincident(g3,g0)
    c: Weight(g1) = 1
    c: Equal(g1,g2)
    c: InternalAlignment(g1,g3)
    c: InternalAlignment(g2,g3)
    c: InternalAlignment(g4,g3)
    c: InternalAlignment(g5,g3)
    c: Block(g3)
    c: Coincident(g6,g0)
    c: Coincident(g6,g3)
    c: Horizontal(g6)
FEATURE [Part::Extrusion] Extrude017  label="caseScrewPillarBracket005"
  Base = -> Sketch023
  Dir = (0,0,1)
  DirMode = 2
  FaceMakerClass = Part::FaceMakerBullseye
  LengthFwd = 2.4
  LengthRev = 0
  Placement = pos=(90.7,29,6.77) rot=(0,-1,0;1.5708rad)
  Solid = true
  Symmetric = false
FEATURE [Sketcher::SketchObject] Sketch024
  FullyConstrained = true
  sketch-geometry (7):
    g0: LineSegment StartX=0 StartY=0 StartZ=0 EndX=0 EndY=6 EndZ=0
    g1: Circle CenterX=0 CenterY=0 CenterZ=0 NormalX=0 NormalY=0 NormalZ=1 AngleXU=0 Radius=1
    g2: Circle CenterX=8 CenterY=6 CenterZ=0 NormalX=0 NormalY=0 NormalZ=1 AngleXU=0 Radius=1
    g3: BSplineCurve PolesCount=3 KnotsCount=2 Degree=2 IsPeriodic=0
    g4: GeomPoint X=0 Y=0 Z=0
    g5: GeomPoint X=8 Y=6 Z=0
    g6: LineSegment StartX=0 StartY=6 StartZ=0 EndX=8 EndY=6 EndZ=0
  constraints (14):
    c: Coincident(g0,g-1)
    c: Distance(g0) = 6
    c: Vertical(g0)
    c: Coincident(g3,g0)
    c: Weight(g1) = 1
    c: Equal(g1,g2)
    c: InternalAlignment(g1,g3)
    c: InternalAlignment(g2,g3)
    c: InternalAlignment(g4,g3)
    c: InternalAlignment(g5,g3)
    c: Block(g3)
    c: Coincident(g6,g0)
    c: Coincident(g6,g3)
    c: Horizontal(g6)
FEATURE [Part::Extrusion] Extrude018  label="caseScrewPillarBracket006"
  Base = -> Sketch024
  Dir = (0,0,1)
  DirMode = 2
  FaceMakerClass = Part::FaceMakerBullseye
  LengthFwd = 2.4
  LengthRev = 0
  Placement = pos=(103.7,29,6.77) rot=(0,-1,0;1.5708rad)
  Solid = true
  Symmetric = false
FEATURE [Sketcher::SketchObject] Sketch025
  FullyConstrained = true
  sketch-geometry (7):
    g0: LineSegment StartX=0 StartY=0 StartZ=0 EndX=0 EndY=6 EndZ=0
    g1: Circle CenterX=0 CenterY=0 CenterZ=0 NormalX=0 NormalY=0 NormalZ=1 AngleXU=0 Radius=1
    g2: Circle CenterX=8 CenterY=6 CenterZ=0 NormalX=0 NormalY=0 NormalZ=1 AngleXU=0 Radius=1
    g3: BSplineCurve PolesCount=3 KnotsCount=2 Degree=2 IsPeriodic=0
    g4: GeomPoint X=0 Y=0 Z=0
    g5: GeomPoint X=8 Y=6 Z=0
    g6: LineSegment StartX=0 StartY=6 StartZ=0 EndX=8 EndY=6 EndZ=0
  constraints (14):
    c: Coincident(g0,g-1)
    c: Distance(g0) = 6
    c: Vertical(g0)
    c: Coincident(g3,g0)
    c: Weight(g1) = 1
    c: Equal(g1,g2)
    c: InternalAlignment(g1,g3)
    c: InternalAlignment(g2,g3)
    c: InternalAlignment(g4,g3)
    c: InternalAlignment(g5,g3)
    c: Block(g3)
    c: Coincident(g6,g0)
    c: Coincident(g6,g3)
    c: Horizontal(g6)
FEATURE [Part::Extrusion] Extrude019  label="caseScrewPillarBracket007"
  Base = -> Sketch025
  Dir = (0,0,1)
  DirMode = 2
  FaceMakerClass = Part::FaceMakerBullseye
  LengthFwd = 2.4
  LengthRev = 0
  Placement = pos=(101.3,29,65.23) rot=(0,1,0;1.5708rad)
  Solid = true
  Symmetric = false
FEATURE [Part::Box] Box011  label="frontCaseScrewPillarBracket"
  AttacherType = Attacher::AttachEngine3D
  Height = 2.4
  Length = 16
  Placement = pos=(87,28,2.3) rot=(0,0,1;0rad)
  Width = 7
FEATURE [Part::Box] Box012  label="frontCaseScrewPillarBracket001"
  AttacherType = Attacher::AttachEngine3D
  Height = 2.4
  Length = 16
  Placement = pos=(87,28,67.3) rot=(0,0,1;0rad)
  Width = 7
FEATURE [Sketcher::SketchObject] Sketch026
  FullyConstrained = true
  sketch-geometry (17):
    g0: Circle CenterX=-3.5 CenterY=23.5 CenterZ=0 NormalX=0 NormalY=0 NormalZ=1 AngleXU=0 Radius=1
    g1: Circle CenterX=-1 CenterY=15.25 CenterZ=0 NormalX=0 NormalY=0 NormalZ=1 AngleXU=0 Radius=1
    g2: Circle CenterX=-3.5 CenterY=7 CenterZ=0 NormalX=0 NormalY=0 NormalZ=1 AngleXU=0 Radius=1
    g3: BSplineCurve PolesCount=3 KnotsCount=2 Degree=2 IsPeriodic=0
    g4: GeomPoint X=-3.5 Y=23.5 Z=0
    g5: GeomPoint X=-3.5 Y=7 Z=0
    g6: Circle CenterX=-4.8 CenterY=30.5 CenterZ=0 NormalX=0 NormalY=0 NormalZ=1 AngleXU=0 Radius=1
    g7: Circle CenterX=-3.5 CenterY=30.5 CenterZ=0 NormalX=0 NormalY=0 NormalZ=1 AngleXU=0 Radius=1
    g8: Circle CenterX=-3.5 CenterY=29.2 CenterZ=0 NormalX=0 NormalY=0 NormalZ=1 AngleXU=0 Radius=1
    g9: BSplineCurve PolesCount=3 KnotsCount=2 Degree=2 IsPeriodic=0
    g10: GeomPoint X=-4.8 Y=30.5 Z=0
    g11: GeomPoint X=-3.5 Y=29.2 Z=0
    g12: LineSegment StartX=-3.5 StartY=29.2 StartZ=0 EndX=-3.5 EndY=23.5 EndZ=0
    g13: LineSegment StartX=-4.8 StartY=30.5 StartZ=0 EndX=0 EndY=30.5 EndZ=0
    g14: LineSegment StartX=-3.5 StartY=5 StartZ=0 EndX=-3.5 EndY=7 EndZ=0
    g15: LineSegment StartX=0 StartY=5 StartZ=0 EndX=0 EndY=30.5 EndZ=0
    g16: LineSegment StartX=-3.5 StartY=5 StartZ=0 EndX=0 EndY=5 EndZ=0
  constraints (33):
    c: Weight(g0) = 1
    c: Equal(g0,g1)
    c: Equal(g0,g2)
    c: InternalAlignment(g0,g3)
    c: InternalAlignment(g1,g3)
    c: InternalAlignment(g2,g3)
    c: InternalAlignment(g4,g3)
    c: InternalAlignment(g5,g3)
    c: Block(g3)
    c: Weight(g6) = 1
    c: Equal(g6,g7)
    c: Equal(g6,g8)
    c: InternalAlignment(g6,g9)
    c: InternalAlignment(g7,g9)
    c: InternalAlignment(g8,g9)
    c: InternalAlignment(g10,g9)
    c: InternalAlignment(g11,g9)
    c: Block(g9)
    c: Coincident(g12,g9)
    c: Coincident(g12,g3)
    c: Vertical(g12)
    c: Coincident(g13,g9)
    c: Horizontal(g13)
    c: Distance(g13) = 4.8
    c: Coincident(g14,g3)
    c: Vertical(g14)
    c: Coincident(g15,g13)
    c: Vertical(g15)
    c: Tangent(g15,g1)
    c: Distance(g14) = 2
    c: Coincident(g16,g14)
    c: Horizontal(g16)
    c: Coincident(g15,g16)
FEATURE [Part::Feature] Face050
  shape: bbox 4.8 x 25.5 x 2e-07 mm, 1 faces, 0 solids (baked)
FEATURE [Part::Revolution] Revolve054  label="moreFrontCaseScrewPost001"
  Angle = 360
  Axis = (0,1,0)
  Base = (0,0,0)
  FaceMakerClass = Part::FaceMakerBullseye
  Placement = pos=(102.5,4.5,3.5) rot=(0,0,1;0rad)
  Solid = false
  Source = -> Face050
  Symmetric = false
FEATURE [Part::Feature] Face051
  shape: bbox 4.8 x 25.5 x 2e-07 mm, 1 faces, 0 solids (baked)
FEATURE [Part::Revolution] Revolve055  label="moreFrontCaseScrewPost002"
  Angle = 360
  Axis = (0,1,0)
  Base = (0,0,0)
  FaceMakerClass = Part::FaceMakerBullseye
  Placement = pos=(102.5,4.5,68.5) rot=(0,0,1;0rad)
  Solid = false
  Source = -> Face051
  Symmetric = false
FEATURE [Sketcher::SketchObject] Sketch027
  FullyConstrained = true
  sketch-geometry (10):
    g0: LineSegment StartX=-1.6 StartY=4.7 StartZ=0 EndX=-1.6 EndY=1.7 EndZ=0
    g1: LineSegment StartX=-3.5 StartY=4.7 StartZ=0 EndX=-1.6 EndY=4.7 EndZ=0
    g2: LineSegment StartX=-1.6 StartY=1.7 StartZ=0 EndX=-1.6 EndY=1.5 EndZ=0
    g3: LineSegment StartX=-1.6 StartY=1.5 StartZ=0 EndX=-5.2 EndY=1.5 EndZ=0
    g4: Circle CenterX=-3.5 CenterY=4.7 CenterZ=0 NormalX=0 NormalY=0 NormalZ=1 AngleXU=0 Radius=1
    g5: Circle CenterX=-3.59627 CenterY=2.99743 CenterZ=0 NormalX=0 NormalY=0 NormalZ=1 AngleXU=0 Radius=1
    g6: Circle CenterX=-5.2 CenterY=1.5 CenterZ=0 NormalX=0 NormalY=0 NormalZ=1 AngleXU=0 Radius=1
    g7: BSplineCurve PolesCount=3 KnotsCount=2 Degree=2 IsPeriodic=0
    g8: GeomPoint X=-3.5 Y=4.7 Z=0
    g9: GeomPoint X=-5.2 Y=1.5 Z=0
  constraints (23):
    c: Vertical(g0)
    c: Distance(g0) = 3
    c: Coincident(g1,g0)
    c: Horizontal(g1)
    c: Block(g0)
    c: Block(g1)
    c: Coincident(g2,g0)
    c: Vertical(g2)
    c: Distance(g2) = 0.2
    c: Coincident(g3,g2)
    c: Horizontal(g3)
    c: Block(g3)
    c: Coincident(g7,g1)
    c: Weight(g4) = 1
    c: Equal(g4,g5)
    c: Equal(g4,g6)
    c: Coincident(g7,g3)
    c: InternalAlignment(g4,g7)
    c: InternalAlignment(g5,g7)
    c: InternalAlignment(g6,g7)
    c: InternalAlignment(g8,g7)
    c: InternalAlignment(g9,g7)
    c: Block(g7)
FEATURE [Sketcher::SketchObject] Sketch028
  FullyConstrained = true
  sketch-geometry (18):
    g0: LineSegment StartX=0 StartY=3e-16 StartZ=0 EndX=0 EndY=1.7 EndZ=0
    g1: LineSegment StartX=-3.5 StartY=0 StartZ=0 EndX=-3.5 EndY=0.9 EndZ=0
    g2: Circle CenterX=-2.7 CenterY=1.7 CenterZ=0 NormalX=0 NormalY=0 NormalZ=1 AngleXU=0 Radius=1
    g3: Circle CenterX=-3.5 CenterY=1.7 CenterZ=0 NormalX=0 NormalY=0 NormalZ=1 AngleXU=0 Radius=1
    g4: Circle CenterX=-3.5 CenterY=0.9 CenterZ=0 NormalX=0 NormalY=0 NormalZ=1 AngleXU=0 Radius=1
    g5: BSplineCurve PolesCount=3 KnotsCount=2 Degree=2 IsPeriodic=0
    g6: GeomPoint X=-2.7 Y=1.7 Z=0
    g7: GeomPoint X=-3.5 Y=0.9 Z=0
    g8: LineSegment StartX=-3.5 StartY=0 StartZ=0 EndX=-3.5 EndY=-7 EndZ=0
    g9: LineSegment StartX=0 StartY=3e-16 StartZ=0 EndX=0 EndY=-7 EndZ=0
    g10: LineSegment StartX=-3.5 StartY=-7 StartZ=0 EndX=0 EndY=-7 EndZ=0
    g11: LineSegment StartX=-2.7 StartY=1.7 StartZ=0 EndX=-1.6 EndY=1.7 EndZ=0
    g12: LineSegment StartX=0 StartY=1.7 StartZ=0 EndX=0 EndY=4.5 EndZ=0
    g13: LineSegment StartX=0 StartY=4.5 StartZ=0 EndX=0 EndY=10.8 EndZ=0
    g14: LineSegment StartX=0 StartY=10.8 StartZ=0 EndX=-2 EndY=10.8 EndZ=0
    g15: LineSegment StartX=-1.6 StartY=4.7 StartZ=0 EndX=-1.6 EndY=1.7 EndZ=0
    g16: LineSegment StartX=-1.6 StartY=4.7 StartZ=0 EndX=-2 EndY=4.7 EndZ=0
    g17: LineSegment StartX=-2 StartY=4.7 StartZ=0 EndX=-2 EndY=10.8 EndZ=0
  constraints (44):
    c: Vertical(g0)
    c: Vertical(g1)
    c: Distance(g1) = 0.9
    c: Block(g0)
    c: Distance(g0) = 1.7
    c: Weight(g2) = 1
    c: Equal(g2,g3)
    c: Equal(g2,g4)
    c: Coincident(g5,g1)
    c: InternalAlignment(g2,g5)
    c: InternalAlignment(g3,g5)
    c: InternalAlignment(g4,g5)
    c: InternalAlignment(g6,g5)
    c: InternalAlignment(g7,g5)
    c: Block(g5)
    c: Coincident(g8,g1)
    c: Vertical(g8)
    c: Distance(g8) = 7
    c: Vertical(g9)
    c: Equal(g8,g9) = 7
    c: Coincident(g9,g0)
    c: Coincident(g10,g8)
    c: Coincident(g10,g9)
    c: Horizontal(g10)
    c: Coincident(g11,g5)
    c: Horizontal(g11)
    c: Coincident(g12,g0)
    c: Vertical(g12)
    c: Distance(g12) = 2.8
    c: Coincident(g13,g12)
    c: Vertical(g13)
    c: Distance(g13) = 6.3
    c: Coincident(g14,g13)
    c: Horizontal(g14)
    c: Distance(g14) = 2
    c: Vertical(g15)
    c: Distance(g15) = 3
    c: Block(g11)
    c: Coincident(g15,g11)
    c: Coincident(g16,g15)
    c: Horizontal(g16)
    c: Coincident(g17,g16)
    c: Coincident(g17,g14)
    c: Vertical(g17)
FEATURE [Part::Revolution] Revolve040  label="backCaseScrewRetainer001"
  Angle = 360
  Axis = (0,1,0)
  Base = (0,0,0)
  FaceMakerClass = Part::FaceMakerBullseye
  Placement = pos=(12.5,3,10) rot=(0,0,1;0rad)
  Solid = false
  Source = -> Face036
  Symmetric = false
FEATURE [Part::Feature] Face055
  shape: bbox 3.5 x 30.2 x 2e-07 mm, 1 faces, 0 solids (baked)
FEATURE [Part::Revolution] Revolve059  label="backCaseScrewPost"
  Angle = 360
  Axis = (0,1,0)
  Base = (0,0,0)
  FaceMakerClass = Part::FaceMakerBullseye
  Placement = pos=(12.5,4.5,10) rot=(0,0,1;0rad)
  Solid = false
  Source = -> Face055
  Symmetric = false
FEATURE [Part::Feature] Face056
  shape: bbox 3.5 x 30.2 x 2e-07 mm, 1 faces, 0 solids (baked)
FEATURE [Part::Revolution] Revolve060  label="backCaseScrewPost001"
  Angle = 360
  Axis = (0,1,0)
  Base = (0,0,0)
  FaceMakerClass = Part::FaceMakerBullseye
  Placement = pos=(12.5,4.5,62) rot=(0,0,1;0rad)
  Solid = false
  Source = -> Face056
  Symmetric = false
FEATURE [Part::Feature] Face057
  shape: bbox 3.5 x 17.8 x 2e-07 mm, 1 faces, 0 solids (baked)
FEATURE [Part::Revolution] Revolve061  label="removeToCreateScrewAndThreadedInsertHole"
  Angle = 360
  Axis = (0,1,0)
  Base = (0,0,0)
  FaceMakerClass = Part::FaceMakerBullseye
  Placement = pos=(12.5,0,10) rot=(0,0,1;0rad)
  Solid = false
  Source = -> Face057
  Symmetric = false
FEATURE [Part::Feature] Face058
  shape: bbox 3.5 x 17.8 x 2e-07 mm, 1 faces, 0 solids (baked)
FEATURE [Part::Revolution] Revolve062  label="removeToCreateScrewAndThreadedInsertHole001"
  Angle = 360
  Axis = (0,1,0)
  Base = (0,0,0)
  FaceMakerClass = Part::FaceMakerBullseye
  Placement = pos=(12.5,0,62) rot=(0,0,1;0rad)
  Solid = false
  Source = -> Face058
  Symmetric = false
FEATURE [Part::Feature] Face059
  shape: bbox 3.5 x 17.8 x 2e-07 mm, 1 faces, 0 solids (baked)
FEATURE [Part::Revolution] Revolve063  label="removeToCreateScrewAndThreadedInsertHole002"
  Angle = 360
  Axis = (0,1,0)
  Base = (0,0,0)
  FaceMakerClass = Part::FaceMakerBullseye
  Placement = pos=(89.5,0,68.5) rot=(0,0,1;0rad)
  Solid = false
  Source = -> Face059
  Symmetric = false
FEATURE [Part::Feature] Face060
  shape: bbox 3.5 x 17.8 x 2e-07 mm, 1 faces, 0 solids (baked)
FEATURE [Part::Revolution] Revolve064  label="removeToCreateScrewAndThreadedInsertHole003"
  Angle = 360
  Axis = (0,1,0)
  Base = (0,0,0)
  FaceMakerClass = Part::FaceMakerBullseye
  Placement = pos=(89.5,0,3.5) rot=(0,0,1;0rad)
  Solid = false
  Source = -> Face060
  Symmetric = false
FEATURE [Part::Feature] Face061
  shape: bbox 3.5 x 17.8 x 2e-07 mm, 1 faces, 0 solids (baked)
FEATURE [Part::Revolution] Revolve065  label="removeToCreateScrewAndThreadedInsertHole004"
  Angle = 360
  Axis = (0,1,0)
  Base = (0,0,0)
  FaceMakerClass = Part::FaceMakerBullseye
  Placement = pos=(102.5,4.7,3.5) rot=(0,0,1;0rad)
  Solid = false
  Source = -> Face061
  Symmetric = false
FEATURE [Part::Feature] Face062
  shape: bbox 3.5 x 17.8 x 2e-07 mm, 1 faces, 0 solids (baked)
FEATURE [Part::Revolution] Revolve066  label="removeToCreateScrewAndThreadedInsertHole005"
  Angle = 360
  Axis = (0,1,0)
  Base = (0,0,0)
  FaceMakerClass = Part::FaceMakerBullseye
  Placement = pos=(102.5,4.7,68.5) rot=(0,0,1;0rad)
  Solid = false
  Source = -> Face062
  Symmetric = false
FEATURE [Part::MultiFuse] Fusion047  label="makeHoles"
  Shapes = -> [Revolve066,Revolve065,Revolve064,Revolve063,Revolve062,Revolve061]
FEATURE [Part::Feature] Face063
  shape: bbox 3.6 x 3.2 x 2e-07 mm, 1 faces, 0 solids (baked)
FEATURE [Part::Revolution] Revolve067  label="moreFrontCaseScrewRetainer002"
  Angle = 360
  Axis = (0,1,0)
  Base = (0,0,0)
  FaceMakerClass = Part::FaceMakerBullseye
  Placement = pos=(102.5,4.5,68.5) rot=(0,0,1;0rad)
  Solid = false
  Source = -> Face063
  Symmetric = false
FEATURE [Part::Feature] Face064
  shape: bbox 3.6 x 3.2 x 2e-07 mm, 1 faces, 0 solids (baked)
FEATURE [Part::Revolution] Revolve068  label="moreFrontCaseScrewRetainer003"
  Angle = 360
  Axis = (0,1,0)
  Base = (0,0,0)
  FaceMakerClass = Part::FaceMakerBullseye
  Placement = pos=(102.5,4.5,3.5) rot=(0,0,1;0rad)
  Solid = false
  Source = -> Face064
  Symmetric = false
FEATURE [Part::Cut] Cut014  label="bottom003"
  Base = -> Cut007
  Tool = -> Fusion047
FEATURE [Part::Feature] Face065
  shape: bbox 3.5 x 17.8 x 2e-07 mm, 1 faces, 0 solids (baked)
FEATURE [Part::Revolution] Revolve069  label="removeToCreateScrewAndThreadedInsertHole006"
  Angle = 360
  Axis = (0,1,0)
  Base = (0,0,0)
  FaceMakerClass = Part::FaceMakerBullseye
  Placement = pos=(12.5,0,10) rot=(0,0,1;0rad)
  Solid = false
  Source = -> Face065
  Symmetric = false
FEATURE [Part::Feature] Face066
  shape: bbox 3.5 x 17.8 x 2e-07 mm, 1 faces, 0 solids (baked)
FEATURE [Part::Revolution] Revolve070  label="removeToCreateScrewAndThreadedInsertHole007"
  Angle = 360
  Axis = (0,1,0)
  Base = (0,0,0)
  FaceMakerClass = Part::FaceMakerBullseye
  Placement = pos=(12.5,0,62) rot=(0,0,1;0rad)
  Solid = false
  Source = -> Face066
  Symmetric = false
FEATURE [Part::Feature] Face067
  shape: bbox 3.5 x 17.8 x 2e-07 mm, 1 faces, 0 solids (baked)
FEATURE [Part::Revolution] Revolve071  label="removeToCreateScrewAndThreadedInsertHole008"
  Angle = 360
  Axis = (0,1,0)
  Base = (0,0,0)
  FaceMakerClass = Part::FaceMakerBullseye
  Placement = pos=(89.5,0,68.5) rot=(0,0,1;0rad)
  Solid = false
  Source = -> Face067
  Symmetric = false
FEATURE [Part::Feature] Face068
  shape: bbox 3.5 x 17.8 x 2e-07 mm, 1 faces, 0 solids (baked)
FEATURE [Part::Revolution] Revolve072  label="removeToCreateScrewAndThreadedInsertHole009"
  Angle = 360
  Axis = (0,1,0)
  Base = (0,0,0)
  FaceMakerClass = Part::FaceMakerBullseye
  Placement = pos=(89.5,0,3.5) rot=(0,0,1;0rad)
  Solid = false
  Source = -> Face068
  Symmetric = false
FEATURE [Part::Feature] Face069
  shape: bbox 3.5 x 17.8 x 2e-07 mm, 1 faces, 0 solids (baked)
FEATURE [Part::Feature] Face070
  shape: bbox 3.5 x 17.8 x 2e-07 mm, 1 faces, 0 solids (baked)
FEATURE [Part::Revolution] Revolve073  label="removeToCreateScrewAndThreadedInsertHole010"
  Angle = 360
  Axis = (0,1,0)
  Base = (0,0,0)
  FaceMakerClass = Part::FaceMakerBullseye
  Placement = pos=(102.5,4.7,3.5) rot=(0,0,1;0rad)
  Solid = false
  Source = -> Face069
  Symmetric = false
FEATURE [Part::Revolution] Revolve074  label="removeToCreateScrewAndThreadedInsertHole011"
  Angle = 360
  Axis = (0,1,0)
  Base = (0,0,0)
  FaceMakerClass = Part::FaceMakerBullseye
  Placement = pos=(102.5,4.7,68.5) rot=(0,0,1;0rad)
  Solid = false
  Source = -> Face070
  Symmetric = false
FEATURE [Part::MultiFuse] Fusion048  label="makeHoles001"
  Shapes = -> [Revolve074,Revolve073,Revolve072,Revolve071,Revolve070,Revolve069]
FEATURE [Part::MultiFuse] Fusion049  label="caseScrewRetainers"
  Shapes = -> [Revolve067,Revolve068,Revolve048,Revolve047,Revolve039,Revolve040]
FEATURE [Part::Cut] Cut015  label="caseScrewRetainers001"
  Base = -> Fusion049
  Tool = -> Fusion048
FEATURE [Part::MultiFuse] Fusion050  label="casePillars"
  Shapes = -> [Revolve055,Revolve054,Revolve043,Revolve046,Revolve059,Revolve060]
FEATURE [Part::Feature] Face071 .. Face076  x6 (patterned run collapsed; names and placements below)
  shape: bbox 3.5 x 17.8 x 2e-07 mm, 1 faces, 0 solids (baked)
FEATURE [Part::Revolution] Revolve075  label="removeToCreateScrewAndThreadedInsertHole012"
  Angle = 360
  Axis = (0,1,0)
  Base = (0,0,0)
  FaceMakerClass = Part::FaceMakerBullseye
  Placement = pos=(12.5,0,10) rot=(0,0,1;0rad)
  Solid = false
  Source = -> Face071
  Symmetric = false
FEATURE [Part::Revolution] Revolve076  label="removeToCreateScrewAndThreadedInsertHole013"
  Angle = 360
  Axis = (0,1,0)
  Base = (0,0,0)
  FaceMakerClass = Part::FaceMakerBullseye
  Placement = pos=(12.5,0,62) rot=(0,0,1;0rad)
  Solid = false
  Source = -> Face072
  Symmetric = false
FEATURE [Part::Revolution] Revolve077  label="removeToCreateScrewAndThreadedInsertHole014"
  Angle = 360
  Axis = (0,1,0)
  Base = (0,0,0)
  FaceMakerClass = Part::FaceMakerBullseye
  Placement = pos=(89.5,0,68.5) rot=(0,0,1;0rad)
  Solid = false
  Source = -> Face073
  Symmetric = false
FEATURE [Part::Revolution] Revolve078  label="removeToCreateScrewAndThreadedInsertHole015"
  Angle = 360
  Axis = (0,1,0)
  Base = (0,0,0)
  FaceMakerClass = Part::FaceMakerBullseye
  Placement = pos=(89.5,0,3.5) rot=(0,0,1;0rad)
  Solid = false
  Source = -> Face074
  Symmetric = false
FEATURE [Part::Revolution] Revolve079  label="removeToCreateScrewAndThreadedInsertHole016"
  Angle = 360
  Axis = (0,1,0)
  Base = (0,0,0)
  FaceMakerClass = Part::FaceMakerBullseye
  Placement = pos=(102.5,4.7,3.5) rot=(0,0,1;0rad)
  Solid = false
  Source = -> Face075
  Symmetric = false
FEATURE [Part::Revolution] Revolve080  label="removeToCreateScrewAndThreadedInsertHole017"
  Angle = 360
  Axis = (0,1,0)
  Base = (0,0,0)
  FaceMakerClass = Part::FaceMakerBullseye
  Placement = pos=(102.5,4.7,68.5) rot=(0,0,1;0rad)
  Solid = false
  Source = -> Face076
  Symmetric = false
FEATURE [Part::MultiFuse] Fusion051  label="makeHoles002"
  Shapes = -> [Revolve080,Revolve079,Revolve078,Revolve077,Revolve076,Revolve075]
FEATURE [Part::Cut] Cut016  label="caesPillars"
  Base = -> Fusion050
  Tool = -> Fusion051
FEATURE [Part::Revolution] Revolve009  label="plugHousing016"
  Angle = 360
  Axis = (0,1,0)
  Base = (0,0,0)
  FaceMakerClass = Part::FaceMakerBullseye
  Placement = pos=(0,0,36.15) rot=(0,0,1;0rad)
  Solid = false
  Source = -> Face012
  Symmetric = false
FEATURE [Part::MultiFuse] Fusion014  label="plugHousing023"
  Placement = pos=(0,0,0) rot=(0,0,1;1.5708rad)
  Shapes = -> [Revolve011,Revolve009]
FEATURE [Part::Revolution] Revolve010  label="plugHousing017"
  Angle = 360
  Axis = (0,1,0)
  Base = (0,0,0)
  FaceMakerClass = Part::FaceMakerBullseye
  Placement = pos=(0,0,36.15) rot=(0,0,1;0rad)
  Solid = false
  Source = -> Face014
  Symmetric = false
FEATURE [Part::MultiFuse] Fusion015  label="plugHousing024"
  Placement = pos=(0,0,0) rot=(0,0,1;1.5708rad)
  Shapes = -> [Revolve010,Revolve015]
FEATURE [Part::Revolution] Revolve014  label="plugHousing026"
  Angle = 360
  Axis = (0,1,0)
  Base = (0,0,0)
  FaceMakerClass = Part::FaceMakerBullseye
  Placement = pos=(0,0,36.15) rot=(0,0,1;0rad)
  Solid = false
  Source = -> Face011
  Symmetric = false
FEATURE [Part::Revolution] Revolve013  label="plugHousing025"
  Angle = 360
  Axis = (0,1,0)
  Base = (0,0,0)
  FaceMakerClass = Part::FaceMakerBullseye
  Placement = pos=(0,0,36.15) rot=(0,0,1;0rad)
  Solid = false
  Source = -> Face015
  Symmetric = false
FEATURE [Part::MultiFuse] Fusion016  label="plugHousing028"
  Placement = pos=(0,19,0) rot=(0,0,1;3.14159rad)
  Shapes = -> [Fusion014,Fusion013]
FEATURE [Part::MultiFuse] Fusion011  label="plugHousing018"
  Placement = pos=(0,0,0) rot=(0,0,1;1.5708rad)
  Shapes = -> [Revolve014,Revolve013]
FEATURE [Part::MultiFuse] Fusion012  label="plugHousing019"
  Placement = pos=(0,19,0) rot=(0,0,1;3.14159rad)
  Shapes = -> [Fusion011,Fusion015]
FEATURE [Part::MultiFuse] Fusion017  label="plugHousing029"
  Placement = pos=(122.621,0,-0.15) rot=(0,0,1;0rad)
  Shapes = -> [Fusion016,Fusion012]
FEATURE [Part::MultiFuse] Fusion052  label="casePillarRetainers"
  Shapes = -> [Extrude012,Extrude013,Extrude014,Extrude015,Extrude016,Extrude017,Extrude018,Extrude019,Box011,Box012]
FEATURE [Part::Feature] Face077
  shape: bbox 3.5 x 17.8 x 2e-07 mm, 1 faces, 0 solids (baked)
FEATURE [Part::Revolution] Revolve081  label="removeToCreateScrewAndThreadedInsertHole018"
  Angle = 360
  Axis = (0,1,0)
  Base = (0,0,0)
  FaceMakerClass = Part::FaceMakerBullseye
  Placement = pos=(62.3,30.3,19.7) rot=(0,0,1;0rad)
  Solid = false
  Source = -> Face077
  Symmetric = false
FEATURE [Part::Feature] Face078
  shape: bbox 3.5 x 17.8 x 2e-07 mm, 1 faces, 0 solids (baked)
FEATURE [Part::Revolution] Revolve082  label="removeToCreateScrewAndThreadedInsertHole019"
  Angle = 360
  Axis = (0,1,0)
  Base = (0,0,0)
  FaceMakerClass = Part::FaceMakerBullseye
  Placement = pos=(62.3,30.3,51.7) rot=(0,0,1;0rad)
  Solid = false
  Source = -> Face078
  Symmetric = false
FEATURE [Part::Feature] Face079
  shape: bbox 3.5 x 17.8 x 2e-07 mm, 1 faces, 0 solids (baked)
FEATURE [Part::Revolution] Revolve083  label="removeToCreateScrewAndThreadedInsertHole020"
  Angle = 360
  Axis = (0,1,0)
  Base = (0,0,0)
  FaceMakerClass = Part::FaceMakerBullseye
  Placement = pos=(30.3,30.3,19.7) rot=(0,0,1;0rad)
  Solid = false
  Source = -> Face079
  Symmetric = false
FEATURE [Part::Feature] Face080
  shape: bbox 3.5 x 17.8 x 2e-07 mm, 1 faces, 0 solids (baked)
FEATURE [Part::Revolution] Revolve084  label="removeToCreateScrewAndThreadedInsertHole021"
  Angle = 360
  Axis = (0,1,0)
  Base = (0,0,0)
  FaceMakerClass = Part::FaceMakerBullseye
  Placement = pos=(30.3,30.3,51.7) rot=(0,0,1;0rad)
  Solid = false
  Source = -> Face080
  Symmetric = false
FEATURE [Part::MultiFuse] Fusion053  label="createThreadedInsertHolesForFan"
  Shapes = -> [Revolve081,Revolve082,Revolve083,Revolve084]
FEATURE [Part::Cut] Cut017  label="fanScrewHousing001"
  Base = -> Fusion046
  Tool = -> Fusion053
FEATURE [Part::Feature] Face081
  shape: bbox 3.5 x 17.8 x 2e-07 mm, 1 faces, 0 solids (baked)
FEATURE [Part::Revolution] Revolve085  label="removeToCreateScrewAndThreadedInsertHole022"
  Angle = 360
  Axis = (0,1,0)
  Base = (0,0,0)
  FaceMakerClass = Part::FaceMakerBullseye
  Placement = pos=(62.3,30.3,19.7) rot=(0,0,1;0rad)
  Solid = false
  Source = -> Face081
  Symmetric = false
FEATURE [Part::Feature] Face082
  shape: bbox 3.5 x 17.8 x 2e-07 mm, 1 faces, 0 solids (baked)
FEATURE [Part::Revolution] Revolve086  label="removeToCreateScrewAndThreadedInsertHole023"
  Angle = 360
  Axis = (0,1,0)
  Base = (0,0,0)
  FaceMakerClass = Part::FaceMakerBullseye
  Placement = pos=(62.3,30.3,51.7) rot=(0,0,1;0rad)
  Solid = false
  Source = -> Face082
  Symmetric = false
FEATURE [Part::Feature] Face083
  shape: bbox 3.5 x 17.8 x 2e-07 mm, 1 faces, 0 solids (baked)
FEATURE [Part::Revolution] Revolve087  label="removeToCreateScrewAndThreadedInsertHole024"
  Angle = 360
  Axis = (0,1,0)
  Base = (0,0,0)
  FaceMakerClass = Part::FaceMakerBullseye
  Placement = pos=(30.3,30.3,19.7) rot=(0,0,1;0rad)
  Solid = false
  Source = -> Face083
  Symmetric = false
FEATURE [Part::Feature] Face084
  shape: bbox 3.5 x 17.8 x 2e-07 mm, 1 faces, 0 solids (baked)
FEATURE [Part::Revolution] Revolve088  label="removeToCreateScrewAndThreadedInsertHole025"
  Angle = 360
  Axis = (0,1,0)
  Base = (0,0,0)
  FaceMakerClass = Part::FaceMakerBullseye
  Placement = pos=(30.3,30.3,51.7) rot=(0,0,1;0rad)
  Solid = false
  Source = -> Face084
  Symmetric = false
FEATURE [Part::MultiFuse] Fusion054  label="createThreadedInsertHolesForFan001"
  Shapes = -> [Revolve085,Revolve086,Revolve087,Revolve088]
FEATURE [Part::Cut] Cut018  label="top007"
  Base = -> Fusion040
  Tool = -> Fusion054
FEATURE [Sketcher::SketchObject] Sketch029
  FullyConstrained = false
  Placement = pos=(0,0,0) rot=(1,0,0;1.5708rad)
  sketch-geometry (24):
    g0: ArcOfCircle CenterX=-4 CenterY=-10.5 CenterZ=0 NormalX=0 NormalY=0 NormalZ=1 AngleXU=0 Radius=1.5 StartAngle=6e-16 EndAngle=3.14159
    g1: ArcOfCircle CenterX=-34.2 CenterY=-10.5 CenterZ=0 NormalX=0 NormalY=0 NormalZ=1 AngleXU=0 Radius=1.5 StartAngle=0 EndAngle=3.14159
    g2: ArcOfCircle CenterX=-34.2 CenterY=-27.7 CenterZ=0 NormalX=0 NormalY=0 NormalZ=1 AngleXU=0 Radius=1.5 StartAngle=3.14159 EndAngle=6.28319
    g3: ArcOfCircle CenterX=-4 CenterY=-27.7 CenterZ=0 NormalX=0 NormalY=0 NormalZ=1 AngleXU=0 Radius=1.5 StartAngle=3.1416 EndAngle=6.28319
    g4: ArcOfCircle CenterX=-10 CenterY=-4.3 CenterZ=0 NormalX=0 NormalY=0 NormalZ=1 AngleXU=0 Radius=1.5 StartAngle=2e-16 EndAngle=3.14159
    g5: ArcOfCircle CenterX=-16.1 CenterY=-1.8 CenterZ=0 NormalX=0 NormalY=0 NormalZ=1 AngleXU=0 Radius=1.5 StartAngle=5e-16 EndAngle=3.14159
    g6: ArcOfCircle CenterX=-22.1 CenterY=-1.8 CenterZ=0 NormalX=0 NormalY=0 NormalZ=1 AngleXU=0 Radius=1.5 StartAngle=5e-16 EndAngle=3.14159
    g7: ArcOfCircle CenterX=-28.2 CenterY=-4.3 CenterZ=0 NormalX=0 NormalY=0 NormalZ=1 AngleXU=0 Radius=1.5 StartAngle=2e-16 EndAngle=3.14159
    g8: ArcOfCircle CenterX=-10 CenterY=-33.9 CenterZ=0 NormalX=0 NormalY=0 NormalZ=1 AngleXU=0 Radius=1.5 StartAngle=3.14159 EndAngle=6.28319
    g9: ArcOfCircle CenterX=-16.1 CenterY=-36.4 CenterZ=0 NormalX=0 NormalY=0 NormalZ=1 AngleXU=0 Radius=1.5 StartAngle=3.14159 EndAngle=6.28319
    g10: ArcOfCircle CenterX=-22.1 CenterY=-36.4 CenterZ=0 NormalX=0 NormalY=0 NormalZ=1 AngleXU=0 Radius=1.5 StartAngle=3.14159 EndAngle=6.28319
    g11: ArcOfCircle CenterX=-28.2 CenterY=-33.9 CenterZ=0 NormalX=0 NormalY=0 NormalZ=1 AngleXU=0 Radius=1.5 StartAngle=3.14159 EndAngle=6.28319
    g12: LineSegment StartX=-35.7 StartY=-10.5 StartZ=0 EndX=-35.7 EndY=-27.7 EndZ=0
    g13: LineSegment StartX=-32.7 StartY=-10.5 StartZ=0 EndX=-32.7 EndY=-27.7 EndZ=0
    g14: LineSegment StartX=-29.7 StartY=-33.9 StartZ=0 EndX=-29.7 EndY=-4.3 EndZ=0
    g15: LineSegment StartX=-26.7 StartY=-33.9 StartZ=0 EndX=-26.7 EndY=-4.3 EndZ=0
    g16: LineSegment StartX=-2.5 StartY=-10.5 StartZ=0 EndX=-2.5 EndY=-27.7 EndZ=0
    g17: LineSegment StartX=-8.5 StartY=-4.3 StartZ=0 EndX=-8.5 EndY=-33.9 EndZ=0
    g18: LineSegment StartX=-5.5 StartY=-10.5 StartZ=0 EndX=-5.5 EndY=-27.7 EndZ=0
    g19: LineSegment StartX=-11.5 StartY=-4.3 StartZ=0 EndX=-11.5 EndY=-33.9 EndZ=0
    g20: LineSegment StartX=-14.6 StartY=-1.8 StartZ=0 EndX=-14.6 EndY=-36.4 EndZ=0
    g21: LineSegment StartX=-17.6 StartY=-1.8 StartZ=0 EndX=-17.6 EndY=-36.4 EndZ=0
    g22: LineSegment StartX=-20.6 StartY=-36.4 StartZ=0 EndX=-20.6 EndY=-1.8 EndZ=0
    g23: LineSegment StartX=-23.6 StartY=-1.8 StartZ=0 EndX=-23.6 EndY=-36.4 EndZ=0
  constraints (48):
    c: Block(g0)
    c: Block(g1)
    c: Block(g2)
    c: Block(g3)
    c: Block(g4)
    c: Block(g5)
    c: Block(g6)
    c: Block(g7)
    c: Block(g8)
    c: Block(g9)
    c: Block(g10)
    c: Block(g11)
    c: Coincident(g12,g1)
    c: Coincident(g12,g2)
    c: Vertical(g12)
    c: Coincident(g13,g1)
    c: Coincident(g13,g2)
    c: Vertical(g13)
    c: Coincident(g14,g11)
    c: Coincident(g14,g7)
    c: Vertical(g14)
    c: Coincident(g15,g11)
    c: Coincident(g15,g7)
    c: Vertical(g15)
    c: Coincident(g16,g0)
    c: Coincident(g16,g3)
    c: Vertical(g16)
    c: Coincident(g17,g4)
    c: Coincident(g17,g8)
    c: Vertical(g17)
    c: Coincident(g18,g0)
    c: Coincident(g18,g3)
    c: Vertical(g18)
    c: Coincident(g19,g4)
    c: Coincident(g19,g8)
    c: Vertical(g19)
    c: Coincident(g20,g5)
    c: Coincident(g20,g9)
    c: Vertical(g20)
    c: Coincident(g21,g5)
    c: Coincident(g21,g9)
    c: Vertical(g21)
    c: Coincident(g22,g10)
    c: Coincident(g22,g6)
    c: Vertical(g22)
    c: Coincident(g23,g6)
    c: Coincident(g23,g10)
    c: Vertical(g23)
FEATURE [Part::Extrusion] Extrude020  label="removeToCreateFanGrillHoles"
  Base = -> Sketch029
  Dir = (0,-1,6e-16)
  DirMode = 2
  FaceMakerClass = Part::FaceMakerBullseye
  LengthFwd = 10
  LengthRev = 0
  Placement = pos=(65.4,44,54.82) rot=(0,0,1;0rad)
  Solid = true
  Symmetric = false
FEATURE [Part::MultiFuse] Fusion055  label="top008"
  Shapes = -> [Cut017,Cut018]
FEATURE [Part::Cut] Cut019  label="top009"
  Base = -> Fusion055
  Tool = -> Extrude020
FEATURE [App::MeasureDistance] Distance003  label="Distance: 71.95 mm"
  Distance = 71.9513
  P1 = (117,38,72)
  P2 = (117,38,0.0487319)
FEATURE [Sketcher::SketchObject] Sketch030
  FullyConstrained = true
  Placement = pos=(117,19,0) rot=(0.57735,0.57735,0.57735;2.0944rad)
  sketch-geometry (48):
    g0: LineSegment StartX=-49.19 StartY=69.25 StartZ=0 EndX=-49.19 EndY=66.25 EndZ=0
    g1: LineSegment StartX=-49.19 StartY=63.5 StartZ=0 EndX=-49.19 EndY=60.5 EndZ=0
    g2: LineSegment StartX=-49.19 StartY=57.75 StartZ=0 EndX=-49.19 EndY=54.75 EndZ=0
    g3: LineSegment StartX=-49.19 StartY=52 StartZ=0 EndX=-49.19 EndY=49 EndZ=0
    g4: LineSegment StartX=-49.19 StartY=46.25 StartZ=0 EndX=-49.19 EndY=43.25 EndZ=0
    g5: LineSegment StartX=-49.19 StartY=40.5 StartZ=0 EndX=-49.19 EndY=37.5 EndZ=0
    g6: LineSegment StartX=-49.19 StartY=34.5 StartZ=0 EndX=-49.19 EndY=31.5 EndZ=0
    g7: LineSegment StartX=-49.19 StartY=28.75 StartZ=0 EndX=-49.19 EndY=25.75 EndZ=0
    g8: LineSegment StartX=-49.19 StartY=23 StartZ=0 EndX=-49.19 EndY=20 EndZ=0
    g9: LineSegment StartX=-49.19 StartY=17.25 StartZ=0 EndX=-49.19 EndY=14.25 EndZ=0
    g10: LineSegment StartX=-49.19 StartY=11.5 StartZ=0 EndX=-49.19 EndY=8.5 EndZ=0
    g11: LineSegment StartX=-49.19 StartY=5.75 StartZ=0 EndX=-49.19 EndY=2.75 EndZ=0
    g12: ArcOfCircle CenterX=-1.5 CenterY=67.75 CenterZ=0 NormalX=0 NormalY=0 NormalZ=1 AngleXU=0 Radius=1.5 StartAngle=4.71239 EndAngle=7.85398
    g13: ArcOfCircle CenterX=-1.5 CenterY=62 CenterZ=0 NormalX=0 NormalY=0 NormalZ=1 AngleXU=0 Radius=1.5 StartAngle=4.71239 EndAngle=7.85398
    g14: ArcOfCircle CenterX=-1.5 CenterY=56.25 CenterZ=0 NormalX=0 NormalY=0 NormalZ=1 AngleXU=0 Radius=1.5 StartAngle=4.71239 EndAngle=7.85398
    g15: ArcOfCircle CenterX=-11.49 CenterY=50.5 CenterZ=0 NormalX=0 NormalY=0 NormalZ=1 AngleXU=0 Radius=1.5 StartAngle=4.71239 EndAngle=7.85398
    g16: ArcOfCircle CenterX=-16.28 CenterY=44.75 CenterZ=0 NormalX=0 NormalY=0 NormalZ=1 AngleXU=0 Radius=1.5 StartAngle=4.71239 EndAngle=7.85398
    g17: ArcOfCircle CenterX=-18.2337 CenterY=39 CenterZ=0 NormalX=0 NormalY=0 NormalZ=1 AngleXU=0 Radius=1.5 StartAngle=4.71485 EndAngle=7.85398
    g18: ArcOfCircle CenterX=-16.2837 CenterY=27.25 CenterZ=0 NormalX=0 NormalY=0 NormalZ=1 AngleXU=0 Radius=1.5 StartAngle=4.71485 EndAngle=7.85398
    g19: ArcOfCircle CenterX=-18.2337 CenterY=33 CenterZ=0 NormalX=0 NormalY=0 NormalZ=1 AngleXU=0 Radius=1.5 StartAngle=4.71485 EndAngle=7.85398
    g20: ArcOfCircle CenterX=-11.49 CenterY=21.5 CenterZ=0 NormalX=0 NormalY=0 NormalZ=1 AngleXU=0 Radius=1.5 StartAngle=4.71239 EndAngle=7.85398
    g21: ArcOfCircle CenterX=-1.5 CenterY=4.25 CenterZ=0 NormalX=0 NormalY=0 NormalZ=1 AngleXU=0 Radius=1.5 StartAngle=4.71239 EndAngle=7.85398
    g22: ArcOfCircle CenterX=-1.5 CenterY=10 CenterZ=0 NormalX=0 NormalY=0 NormalZ=1 AngleXU=0 Radius=1.5 StartAngle=4.71239 EndAngle=7.85398
    g23: ArcOfCircle CenterX=-1.5 CenterY=15.75 CenterZ=0 NormalX=0 NormalY=0 NormalZ=1 AngleXU=0 Radius=1.5 StartAngle=4.71239 EndAngle=7.85398
    g24: LineSegment StartX=-49.19 StartY=69.25 StartZ=0 EndX=-1.5 EndY=69.25 EndZ=0
    g25: LineSegment StartX=-49.19 StartY=66.25 StartZ=0 EndX=-1.5 EndY=66.25 EndZ=0
    g26: LineSegment StartX=-49.19 StartY=63.5 StartZ=0 EndX=-1.5 EndY=63.5 EndZ=0
    g27: LineSegment StartX=-49.19 StartY=60.5 StartZ=0 EndX=-1.5 EndY=60.5 EndZ=0
    g28: LineSegment StartX=-49.19 StartY=57.75 StartZ=0 EndX=-1.5 EndY=57.75 EndZ=0
    g29: LineSegment StartX=-49.19 StartY=54.75 StartZ=0 EndX=-1.5 EndY=54.75 EndZ=0
    g30: LineSegment StartX=-49.19 StartY=52 StartZ=0 EndX=-11.49 EndY=52 EndZ=0
    g31: LineSegment StartX=-49.19 StartY=49 StartZ=0 EndX=-11.49 EndY=49 EndZ=0
    g32: LineSegment StartX=-49.19 StartY=46.25 StartZ=0 EndX=-16.28 EndY=46.25 EndZ=0
    g33: LineSegment StartX=-49.19 StartY=43.25 StartZ=0 EndX=-16.28 EndY=43.25 EndZ=0
    g34: LineSegment StartX=-49.19 StartY=40.5 StartZ=0 EndX=-18.2337 EndY=40.5 EndZ=0
    g35: LineSegment StartX=-49.19 StartY=37.5 StartZ=0 EndX=-18.23 EndY=37.5 EndZ=0
    g36: LineSegment StartX=-49.19 StartY=34.5 StartZ=0 EndX=-18.2337 EndY=34.5 EndZ=0
    g37: LineSegment StartX=-49.19 StartY=31.5 StartZ=0 EndX=-18.23 EndY=31.5 EndZ=0
    g38: LineSegment StartX=-49.19 StartY=28.75 StartZ=0 EndX=-16.2837 EndY=28.75 EndZ=0
    g39: LineSegment StartX=-49.19 StartY=25.75 StartZ=0 EndX=-16.28 EndY=25.75 EndZ=0
    g40: LineSegment StartX=-49.19 StartY=23 StartZ=0 EndX=-11.49 EndY=23 EndZ=0
    g41: LineSegment StartX=-49.19 StartY=20 StartZ=0 EndX=-11.49 EndY=20 EndZ=0
    g42: LineSegment StartX=-49.19 StartY=17.25 StartZ=0 EndX=-1.5 EndY=17.25 EndZ=0
    g43: LineSegment StartX=-49.19 StartY=14.25 StartZ=0 EndX=-1.5 EndY=14.25 EndZ=0
    g44: LineSegment StartX=-49.19 StartY=11.5 StartZ=0 EndX=-1.5 EndY=11.5 EndZ=0
    g45: LineSegment StartX=-49.19 StartY=8.5 StartZ=0 EndX=-1.5 EndY=8.5 EndZ=0
    g46: LineSegment StartX=-49.19 StartY=5.75 StartZ=0 EndX=-1.5 EndY=5.75 EndZ=0
    g47: LineSegment StartX=-49.19 StartY=2.75 StartZ=0 EndX=-1.5 EndY=2.75 EndZ=0
  constraints (120):
    c: Vertical(g0)
    c: Distance(g0) = 3
    c: Block(g0)
    c: Vertical(g1)
    c: Distance(g1) = 3
    c: Vertical(g2)
    c: Equal(g0,g2) = 3
    c: Block(g2)
    c: Vertical(g3)
    c: Equal(g1,g3) = 3
    c: Vertical(g4)
    c: Equal(g0,g4) = 3
    c: Block(g4)
    c: Vertical(g5)
    c: Equal(g1,g5) = 3
    c: Vertical(g6)
    c: Equal(g0,g6) = 3
    c: Block(g6)
    c: Vertical(g7)
    c: Equal(g1,g7) = 3
    c: Vertical(g8)
    c: Equal(g0,g8) = 3
    c: Block(g8)
    c: Vertical(g9)
    c: Equal(g1,g9) = 3
    c: Vertical(g10)
    c: Equal(g0,g10) = 3
    c: Block(g10)
    c: Vertical(g11)
    c: Equal(g1,g11) = 3
    c: Block(g12)
    c: Block(g13)
    c: Block(g14)
    c: Block(g15)
    c: Block(g16)
    c: Block(g17)
    c: Block(g18)
    c: Block(g19)
    c: Block(g20)
    c: Block(g21)
    c: Block(g22)
    c: Block(g23)
    c: Block(g11)
    c: Block(g9)
    c: Block(g7)
    c: Block(g5)
    c: Block(g3)
    c: Block(g1)
    c: Coincident(g24,g0)
    c: Coincident(g24,g12)
    c: Horizontal(g24)
    c: Coincident(g25,g0)
    c: Coincident(g25,g12)
    c: Horizontal(g25)
    c: Coincident(g26,g1)
    c: Coincident(g26,g13)
    c: Horizontal(g26)
    c: Coincident(g27,g1)
    c: Coincident(g27,g13)
    c: Horizontal(g27)
    c: Coincident(g28,g2)
    c: Coincident(g28,g14)
    c: Horizontal(g28)
    c: Coincident(g29,g2)
    c: Coincident(g29,g14)
    c: Horizontal(g29)
    c: Coincident(g30,g3)
    c: Coincident(g30,g15)
    c: Horizontal(g30)
    c: Coincident(g31,g3)
    c: Coincident(g31,g15)
    c: Horizontal(g31)
    c: Coincident(g32,g4)
    c: Coincident(g32,g16)
    c: Horizontal(g32)
    c: Coincident(g33,g4)
    c: Coincident(g33,g16)
    c: Horizontal(g33)
    c: Coincident(g34,g5)
    c: Coincident(g34,g17)
    c: Horizontal(g34)
    c: Coincident(g35,g5)
    c: Coincident(g35,g17)
    c: Horizontal(g35)
    c: Coincident(g36,g6)
    c: Coincident(g36,g19)
    c: Horizontal(g36)
    c: Coincident(g37,g6)
    c: Coincident(g37,g19)
    c: Horizontal(g37)
    c: Coincident(g38,g7)
    c: Coincident(g38,g18)
    c: Horizontal(g38)
    c: Coincident(g39,g7)
    c: Coincident(g39,g18)
    c: Horizontal(g39)
    c: Coincident(g40,g8)
    c: Coincident(g40,g20)
    c: Horizontal(g40)
    c: Coincident(g41,g8)
    c: Coincident(g41,g20)
    c: Horizontal(g41)
    c: Coincident(g42,g9)
    c: Coincident(g42,g23)
    c: Horizontal(g42)
    c: Coincident(g43,g9)
    c: Coincident(g43,g23)
    c: Horizontal(g43)
    c: Coincident(g44,g10)
    c: Coincident(g44,g22)
    c: Horizontal(g44)
    c: Coincident(g45,g10)
    c: Coincident(g45,g22)
    c: Horizontal(g45)
    c: Coincident(g46,g11)
    c: Coincident(g46,g21)
    c: Horizontal(g46)
    c: Coincident(g47,g11)
    c: Coincident(g47,g21)
    c: Horizontal(g47)
FEATURE [Sketcher::SketchObject] Sketch031
  FullyConstrained = true
  Placement = pos=(117,19,0) rot=(0.57735,0.57735,0.57735;2.0944rad)
  sketch-geometry (24):
    g0: ArcOfCircle CenterX=-49.19 CenterY=67.75 CenterZ=0 NormalX=0 NormalY=0 NormalZ=1 AngleXU=0 Radius=1.5 StartAngle=1.5708 EndAngle=4.71239
    g1: ArcOfCircle CenterX=-49.19 CenterY=62 CenterZ=0 NormalX=0 NormalY=0 NormalZ=1 AngleXU=0 Radius=1.5 StartAngle=1.5708 EndAngle=4.71239
    g2: ArcOfCircle CenterX=-49.19 CenterY=56.25 CenterZ=0 NormalX=0 NormalY=0 NormalZ=1 AngleXU=0 Radius=1.5 StartAngle=1.5708 EndAngle=4.71239
    g3: ArcOfCircle CenterX=-49.19 CenterY=50.5 CenterZ=0 NormalX=0 NormalY=0 NormalZ=1 AngleXU=0 Radius=1.5 StartAngle=1.5708 EndAngle=4.71239
    g4: ArcOfCircle CenterX=-49.19 CenterY=44.75 CenterZ=0 NormalX=0 NormalY=0 NormalZ=1 AngleXU=0 Radius=1.5 StartAngle=1.5708 EndAngle=4.71239
    g5: ArcOfCircle CenterX=-49.19 CenterY=39 CenterZ=0 NormalX=0 NormalY=0 NormalZ=1 AngleXU=0 Radius=1.5 StartAngle=1.5708 EndAngle=4.71239
    g6: ArcOfCircle CenterX=-49.19 CenterY=33 CenterZ=0 NormalX=0 NormalY=0 NormalZ=1 AngleXU=0 Radius=1.5 StartAngle=1.5708 EndAngle=4.71239
    g7: ArcOfCircle CenterX=-49.19 CenterY=27.25 CenterZ=0 NormalX=0 NormalY=0 NormalZ=1 AngleXU=0 Radius=1.5 StartAngle=1.5708 EndAngle=4.71239
    g8: ArcOfCircle CenterX=-49.19 CenterY=21.5 CenterZ=0 NormalX=0 NormalY=0 NormalZ=1 AngleXU=0 Radius=1.5 StartAngle=1.5708 EndAngle=4.71239
    g9: ArcOfCircle CenterX=-49.19 CenterY=15.75 CenterZ=0 NormalX=0 NormalY=0 NormalZ=1 AngleXU=0 Radius=1.5 StartAngle=1.5708 EndAngle=4.71239
    g10: ArcOfCircle CenterX=-49.19 CenterY=10 CenterZ=0 NormalX=0 NormalY=0 NormalZ=1 AngleXU=0 Radius=1.5 StartAngle=1.5708 EndAngle=4.71239
    g11: ArcOfCircle CenterX=-49.19 CenterY=4.25 CenterZ=0 NormalX=0 NormalY=0 NormalZ=1 AngleXU=0 Radius=1.5 StartAngle=1.5708 EndAngle=4.71239
    g12: LineSegment StartX=-49.19 StartY=69.25 StartZ=0 EndX=-49.19 EndY=66.25 EndZ=0
    g13: LineSegment StartX=-49.19 StartY=63.5 StartZ=0 EndX=-49.19 EndY=60.5 EndZ=0
    g14: LineSegment StartX=-49.19 StartY=57.75 StartZ=0 EndX=-49.19 EndY=54.75 EndZ=0
    g15: LineSegment StartX=-49.19 StartY=52 StartZ=0 EndX=-49.19 EndY=49 EndZ=0
    g16: LineSegment StartX=-49.19 StartY=46.25 StartZ=0 EndX=-49.19 EndY=43.25 EndZ=0
    g17: LineSegment StartX=-49.19 StartY=40.5 StartZ=0 EndX=-49.19 EndY=37.5 EndZ=0
    g18: LineSegment StartX=-49.19 StartY=34.5 StartZ=0 EndX=-49.19 EndY=31.5 EndZ=0
    g19: LineSegment StartX=-49.19 StartY=28.75 StartZ=0 EndX=-49.19 EndY=25.75 EndZ=0
    g20: LineSegment StartX=-49.19 StartY=23 StartZ=0 EndX=-49.19 EndY=20 EndZ=0
    g21: LineSegment StartX=-49.19 StartY=17.25 StartZ=0 EndX=-49.19 EndY=14.25 EndZ=0
    g22: LineSegment StartX=-49.19 StartY=11.5 StartZ=0 EndX=-49.19 EndY=8.5 EndZ=0
    g23: LineSegment StartX=-49.19 StartY=5.75 StartZ=0 EndX=-49.19 EndY=2.75 EndZ=0
  constraints (48):
    c: Block(g0)
    c: Block(g1)
    c: Block(g2)
    c: Block(g3)
    c: Block(g4)
    c: Block(g5)
    c: Block(g6)
    c: Block(g7)
    c: Block(g8)
    c: Block(g9)
    c: Block(g10)
    c: Block(g11)
    c: Coincident(g12,g0)
    c: Coincident(g12,g0)
    c: Vertical(g12)
    c: Vertical(g13)
    c: Coincident(g13,g1)
    c: Vertical(g14)
    c: Coincident(g14,g2)
    c: Vertical(g15)
    c: Coincident(g15,g3)
    c: Vertical(g16)
    c: Coincident(g16,g4)
    c: Vertical(g17)
    c: Coincident(g17,g5)
    c: Vertical(g18)
    c: Coincident(g18,g6)
    c: Vertical(g19)
    c: Coincident(g19,g7)
    c: Vertical(g20)
    c: Coincident(g20,g8)
    c: Vertical(g21)
    c: Coincident(g21,g9)
    c: Vertical(g22)
    c: Coincident(g22,g10)
    c: Vertical(g23)
    c: Coincident(g23,g11)
    c: Block(g23)
    c: Block(g22)
    c: Block(g21)
    c: Block(g20)
    c: Block(g13)
    c: Block(g14)
    c: Block(g15)
    c: Block(g16)
    c: Block(g17)
    c: Block(g18)
    c: Block(g19)
FEATURE [Part::Extrusion] Extrude022
  Base = -> Sketch030
  Dir = (1,-2e-16,2e-16)
  DirMode = 2
  FaceMakerClass = Part::FaceMakerBullseye
  LengthFwd = 19
  LengthRev = 0
  Placement = pos=(-19,0,0) rot=(0,0,1;0rad)
  Solid = true
  Symmetric = false
FEATURE [Part::Fillet] Fillet022
  Base = -> Extrude022
  Edges = 24 edges r=1.49: [Edge6,Edge11,Edge18,Edge23,Edge30,Edge35,Edge42,Edge47,Edge54,Edge59,Edge66,Edge71,Edge78,Edge83,Edge90,Edge95,Edge102,Edge107,Edge114,Edge119,Edge126,Edge131,Edge138,Edge143]
FEATURE [Part::Cut] Cut020
  Base = -> Cut019
  Tool = -> Fillet022
FEATURE [Sketcher::SketchObject] Sketch032
  FullyConstrained = true
  Placement = pos=(117,19,0) rot=(0.57735,0.57735,0.57735;2.0944rad)
  sketch-geometry (48):
    g0: LineSegment StartX=-49.19 StartY=69.25 StartZ=0 EndX=-49.19 EndY=66.25 EndZ=0
    g1: LineSegment StartX=-49.19 StartY=63.5 StartZ=0 EndX=-49.19 EndY=60.5 EndZ=0
    g2: LineSegment StartX=-49.19 StartY=57.75 StartZ=0 EndX=-49.19 EndY=54.75 EndZ=0
    g3: LineSegment StartX=-49.19 StartY=52 StartZ=0 EndX=-49.19 EndY=49 EndZ=0
    g4: LineSegment StartX=-49.19 StartY=46.25 StartZ=0 EndX=-49.19 EndY=43.25 EndZ=0
    g5: LineSegment StartX=-49.19 StartY=40.5 StartZ=0 EndX=-49.19 EndY=37.5 EndZ=0
    g6: LineSegment StartX=-49.19 StartY=34.5 StartZ=0 EndX=-49.19 EndY=31.5 EndZ=0
    g7: LineSegment StartX=-49.19 StartY=28.75 StartZ=0 EndX=-49.19 EndY=25.75 EndZ=0
    g8: LineSegment StartX=-49.19 StartY=23 StartZ=0 EndX=-49.19 EndY=20 EndZ=0
    g9: LineSegment StartX=-49.19 StartY=17.25 StartZ=0 EndX=-49.19 EndY=14.25 EndZ=0
    g10: LineSegment StartX=-49.19 StartY=11.5 StartZ=0 EndX=-49.19 EndY=8.5 EndZ=0
    g11: LineSegment StartX=-49.19 StartY=5.75 StartZ=0 EndX=-49.19 EndY=2.75 EndZ=0
    g12: ArcOfCircle CenterX=-1.5 CenterY=67.75 CenterZ=0 NormalX=0 NormalY=0 NormalZ=1 AngleXU=0 Radius=1.5 StartAngle=4.71239 EndAngle=7.85398
    g13: ArcOfCircle CenterX=-1.5 CenterY=62 CenterZ=0 NormalX=0 NormalY=0 NormalZ=1 AngleXU=0 Radius=1.5 StartAngle=4.71239 EndAngle=7.85398
    g14: ArcOfCircle CenterX=-1.5 CenterY=56.25 CenterZ=0 NormalX=0 NormalY=0 NormalZ=1 AngleXU=0 Radius=1.5 StartAngle=4.71239 EndAngle=7.85398
    g15: ArcOfCircle CenterX=-11.49 CenterY=50.5 CenterZ=0 NormalX=0 NormalY=0 NormalZ=1 AngleXU=0 Radius=1.5 StartAngle=4.71239 EndAngle=7.85398
    g16: ArcOfCircle CenterX=-16.28 CenterY=44.75 CenterZ=0 NormalX=0 NormalY=0 NormalZ=1 AngleXU=0 Radius=1.5 StartAngle=4.71239 EndAngle=7.85398
    g17: ArcOfCircle CenterX=-18.2337 CenterY=39 CenterZ=0 NormalX=0 NormalY=0 NormalZ=1 AngleXU=0 Radius=1.5 StartAngle=4.71485 EndAngle=7.85398
    g18: ArcOfCircle CenterX=-16.2837 CenterY=27.25 CenterZ=0 NormalX=0 NormalY=0 NormalZ=1 AngleXU=0 Radius=1.5 StartAngle=4.71485 EndAngle=7.85398
    g19: ArcOfCircle CenterX=-18.2337 CenterY=33 CenterZ=0 NormalX=0 NormalY=0 NormalZ=1 AngleXU=0 Radius=1.5 StartAngle=4.71485 EndAngle=7.85398
    g20: ArcOfCircle CenterX=-11.49 CenterY=21.5 CenterZ=0 NormalX=0 NormalY=0 NormalZ=1 AngleXU=0 Radius=1.5 StartAngle=4.71239 EndAngle=7.85398
    g21: ArcOfCircle CenterX=-1.5 CenterY=4.25 CenterZ=0 NormalX=0 NormalY=0 NormalZ=1 AngleXU=0 Radius=1.5 StartAngle=4.71239 EndAngle=7.85398
    g22: ArcOfCircle CenterX=-1.5 CenterY=10 CenterZ=0 NormalX=0 NormalY=0 NormalZ=1 AngleXU=0 Radius=1.5 StartAngle=4.71239 EndAngle=7.85398
    g23: ArcOfCircle CenterX=-1.5 CenterY=15.75 CenterZ=0 NormalX=0 NormalY=0 NormalZ=1 AngleXU=0 Radius=1.5 StartAngle=4.71239 EndAngle=7.85398
    g24: LineSegment StartX=-49.19 StartY=69.25 StartZ=0 EndX=-1.5 EndY=69.25 EndZ=0
    g25: LineSegment StartX=-49.19 StartY=66.25 StartZ=0 EndX=-1.5 EndY=66.25 EndZ=0
    g26: LineSegment StartX=-49.19 StartY=63.5 StartZ=0 EndX=-1.5 EndY=63.5 EndZ=0
    g27: LineSegment StartX=-49.19 StartY=60.5 StartZ=0 EndX=-1.5 EndY=60.5 EndZ=0
    g28: LineSegment StartX=-49.19 StartY=57.75 StartZ=0 EndX=-1.5 EndY=57.75 EndZ=0
    g29: LineSegment StartX=-49.19 StartY=54.75 StartZ=0 EndX=-1.5 EndY=54.75 EndZ=0
    g30: LineSegment StartX=-49.19 StartY=52 StartZ=0 EndX=-11.49 EndY=52 EndZ=0
    g31: LineSegment StartX=-49.19 StartY=49 StartZ=0 EndX=-11.49 EndY=49 EndZ=0
    g32: LineSegment StartX=-49.19 StartY=46.25 StartZ=0 EndX=-16.28 EndY=46.25 EndZ=0
    g33: LineSegment StartX=-49.19 StartY=43.25 StartZ=0 EndX=-16.28 EndY=43.25 EndZ=0
    g34: LineSegment StartX=-49.19 StartY=40.5 StartZ=0 EndX=-18.2337 EndY=40.5 EndZ=0
    g35: LineSegment StartX=-49.19 StartY=37.5 StartZ=0 EndX=-18.23 EndY=37.5 EndZ=0
    g36: LineSegment StartX=-49.19 StartY=34.5 StartZ=0 EndX=-18.2337 EndY=34.5 EndZ=0
    g37: LineSegment StartX=-49.19 StartY=31.5 StartZ=0 EndX=-18.23 EndY=31.5 EndZ=0
    g38: LineSegment StartX=-49.19 StartY=28.75 StartZ=0 EndX=-16.2837 EndY=28.75 EndZ=0
    g39: LineSegment StartX=-49.19 StartY=25.75 StartZ=0 EndX=-16.28 EndY=25.75 EndZ=0
    g40: LineSegment StartX=-49.19 StartY=23 StartZ=0 EndX=-11.49 EndY=23 EndZ=0
    g41: LineSegment StartX=-49.19 StartY=20 StartZ=0 EndX=-11.49 EndY=20 EndZ=0
    g42: LineSegment StartX=-49.19 StartY=17.25 StartZ=0 EndX=-1.5 EndY=17.25 EndZ=0
    g43: LineSegment StartX=-49.19 StartY=14.25 StartZ=0 EndX=-1.5 EndY=14.25 EndZ=0
    g44: LineSegment StartX=-49.19 StartY=11.5 StartZ=0 EndX=-1.5 EndY=11.5 EndZ=0
    g45: LineSegment StartX=-49.19 StartY=8.5 StartZ=0 EndX=-1.5 EndY=8.5 EndZ=0
    g46: LineSegment StartX=-49.19 StartY=5.75 StartZ=0 EndX=-1.5 EndY=5.75 EndZ=0
    g47: LineSegment StartX=-49.19 StartY=2.75 StartZ=0 EndX=-1.5 EndY=2.75 EndZ=0
  constraints (120):
    c: Vertical(g0)
    c: Distance(g0) = 3
    c: Block(g0)
    c: Vertical(g1)
    c: Distance(g1) = 3
    c: Vertical(g2)
    c: Equal(g0,g2) = 3
    c: Block(g2)
    c: Vertical(g3)
    c: Equal(g1,g3) = 3
    c: Vertical(g4)
    c: Equal(g0,g4) = 3
    c: Block(g4)
    c: Vertical(g5)
    c: Equal(g1,g5) = 3
    c: Vertical(g6)
    c: Equal(g0,g6) = 3
    c: Block(g6)
    c: Vertical(g7)
    c: Equal(g1,g7) = 3
    c: Vertical(g8)
    c: Equal(g0,g8) = 3
    c: Block(g8)
    c: Vertical(g9)
    c: Equal(g1,g9) = 3
    c: Vertical(g10)
    c: Equal(g0,g10) = 3
    c: Block(g10)
    c: Vertical(g11)
    c: Equal(g1,g11) = 3
    c: Block(g12)
    c: Block(g13)
    c: Block(g14)
    c: Block(g15)
    c: Block(g16)
    c: Block(g17)
    c: Block(g18)
    c: Block(g19)
    c: Block(g20)
    c: Block(g21)
    c: Block(g22)
    c: Block(g23)
    c: Block(g11)
    c: Block(g9)
    c: Block(g7)
    c: Block(g5)
    c: Block(g3)
    c: Block(g1)
    c: Coincident(g24,g0)
    c: Coincident(g24,g12)
    c: Horizontal(g24)
    c: Coincident(g25,g0)
    c: Coincident(g25,g12)
    c: Horizontal(g25)
    c: Coincident(g26,g1)
    c: Coincident(g26,g13)
    c: Horizontal(g26)
    c: Coincident(g27,g1)
    c: Coincident(g27,g13)
    c: Horizontal(g27)
    c: Coincident(g28,g2)
    c: Coincident(g28,g14)
    c: Horizontal(g28)
    c: Coincident(g29,g2)
    c: Coincident(g29,g14)
    c: Horizontal(g29)
    c: Coincident(g30,g3)
    c: Coincident(g30,g15)
    c: Horizontal(g30)
    c: Coincident(g31,g3)
    c: Coincident(g31,g15)
    c: Horizontal(g31)
    c: Coincident(g32,g4)
    c: Coincident(g32,g16)
    c: Horizontal(g32)
    c: Coincident(g33,g4)
    c: Coincident(g33,g16)
    c: Horizontal(g33)
    c: Coincident(g34,g5)
    c: Coincident(g34,g17)
    c: Horizontal(g34)
    c: Coincident(g35,g5)
    c: Coincident(g35,g17)
    c: Horizontal(g35)
    c: Coincident(g36,g6)
    c: Coincident(g36,g19)
    c: Horizontal(g36)
    c: Coincident(g37,g6)
    c: Coincident(g37,g19)
    c: Horizontal(g37)
    c: Coincident(g38,g7)
    c: Coincident(g38,g18)
    c: Horizontal(g38)
    c: Coincident(g39,g7)
    c: Coincident(g39,g18)
    c: Horizontal(g39)
    c: Coincident(g40,g8)
    c: Coincident(g40,g20)
    c: Horizontal(g40)
    c: Coincident(g41,g8)
    c: Coincident(g41,g20)
    c: Horizontal(g41)
    c: Coincident(g42,g9)
    c: Coincident(g42,g23)
    c: Horizontal(g42)
    c: Coincident(g43,g9)
    c: Coincident(g43,g23)
    c: Horizontal(g43)
    c: Coincident(g44,g10)
    c: Coincident(g44,g22)
    c: Horizontal(g44)
    c: Coincident(g45,g10)
    c: Coincident(g45,g22)
    c: Horizontal(g45)
    c: Coincident(g46,g11)
    c: Coincident(g46,g21)
    c: Horizontal(g46)
    c: Coincident(g47,g11)
    c: Coincident(g47,g21)
    c: Horizontal(g47)
FEATURE [Part::Extrusion] Extrude023
  Base = -> Sketch032
  Dir = (1,-2e-16,2e-16)
  DirMode = 2
  FaceMakerClass = Part::FaceMakerBullseye
  LengthFwd = 19
  LengthRev = 0
  Placement = pos=(-19,0,0) rot=(0,0,1;0rad)
  Solid = true
  Symmetric = false
FEATURE [Part::Fillet] Fillet023
  Base = -> Extrude023
  Edges = 24 edges r=1.49: [Edge6,Edge11,Edge18,Edge23,Edge30,Edge35,Edge42,Edge47,Edge54,Edge59,Edge66,Edge71,Edge78,Edge83,Edge90,Edge95,Edge102,Edge107,Edge114,Edge119,Edge126,Edge131,Edge138,Edge143]
